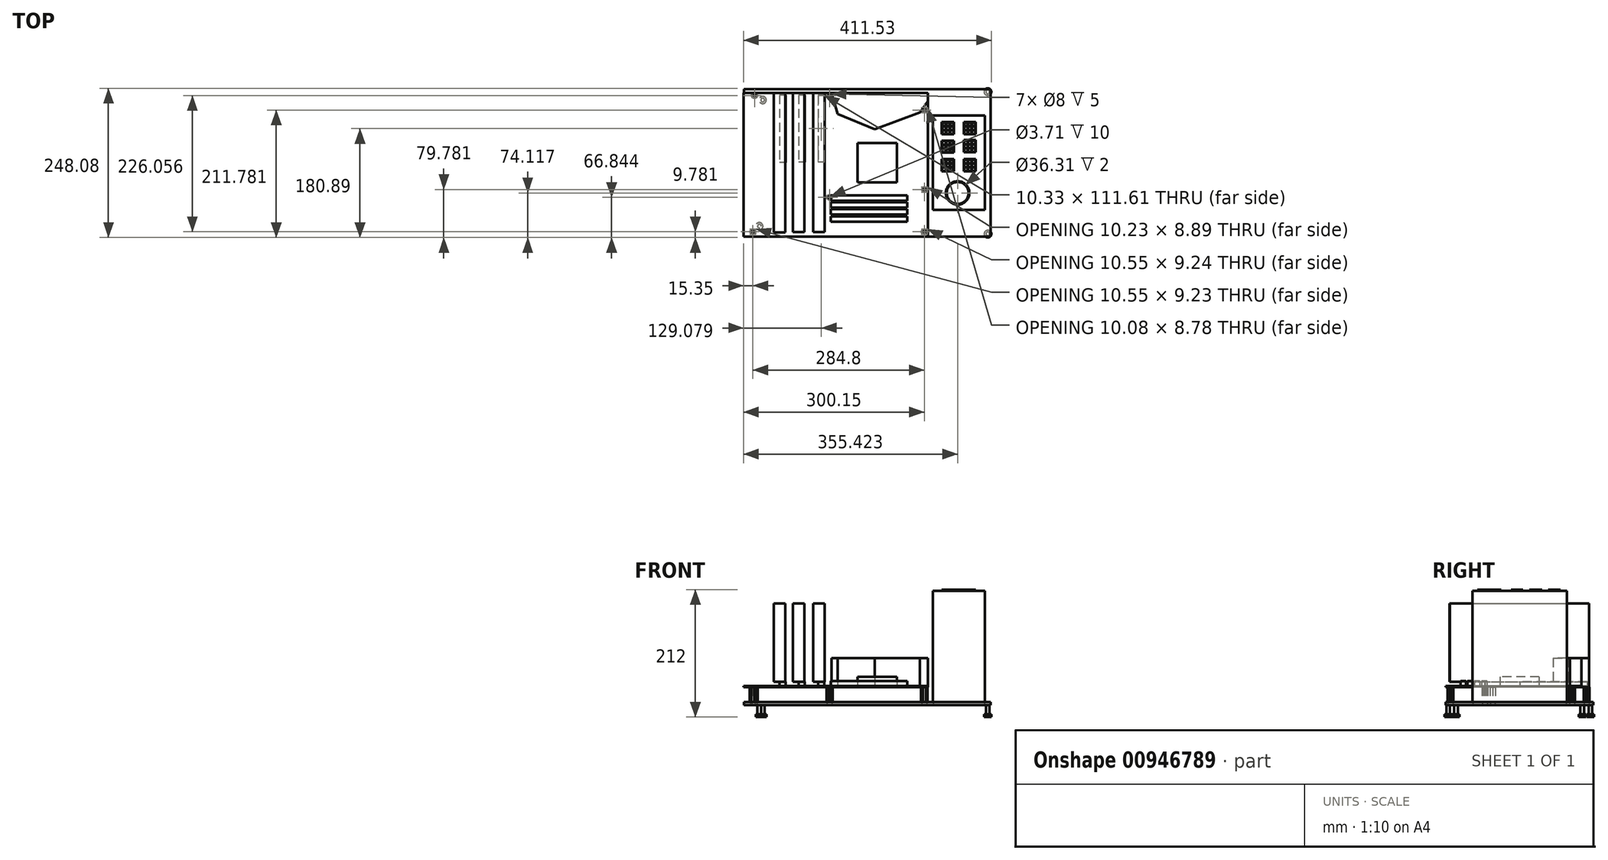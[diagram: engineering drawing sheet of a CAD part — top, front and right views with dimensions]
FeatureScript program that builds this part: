
annotation { "Feature Type Name" : "Feature", "Feature Type Description" : "" }
export const myFeature = defineFeature(function(context is Context, id is Id, definition is map)
    precondition{}
    {
        {
            var Q0;
            Q0=qCreatedBy(makeId("Top.planeOp"),FACE);
            var sketch = newSketch(context, id + "F0", { "sketchPlane" : qUnion([Q0])});
            skLineSegment(sketch, "E0.bottom", {"start": v(-235.28, 113.95) * mm, "end": v(174.52, 113.95) * mm});
            skLineSegment(sketch, "E0.top", {"start": v(-235.28, -131.05) * mm, "end": v(174.52, -131.05) * mm});
            skLineSegment(sketch, "E0.left", {"start": v(-235.28, 113.95) * mm, "end": v(-235.28, -131.05) * mm});
            skLineSegment(sketch, "E0.right", {"start": v(174.52, 113.95) * mm, "end": v(174.52, -131.05) * mm});
            skLineSegment(sketch, "E1", {"start": v(69.52, 113.95) * mm, "end": v(69.52, -131.05) * mm});
            skLineSegment(sketch, "E2.bottom", {"start": v(164.52, 68.95) * mm, "end": v(79.52, 68.95) * mm});
            skLineSegment(sketch, "E2.top", {"start": v(164.52, -86.05) * mm, "end": v(79.52, -86.05) * mm});
            skLineSegment(sketch, "E2.left", {"start": v(164.52, 68.95) * mm, "end": v(164.52, -86.05) * mm});
            skLineSegment(sketch, "E2.right", {"start": v(79.52, 68.95) * mm, "end": v(79.52, -86.05) * mm});
            skCircle(sketch, "E3", {"center": v(-217.38, 103) * mm, "radius": 4 * mm});
            skCircle(sketch, "E4", {"center": v(64.52, 78.95) * mm, "radius": 4 * mm});
            skCircle(sketch, "E5", {"center": v(64.52, -53.05) * mm, "radius": 4 * mm});
            skCircle(sketch, "E6", {"center": v(64.52, -123.05) * mm, "radius": 4 * mm});
            skCircle(sketch, "E7", {"center": v(-92.98, -66.08) * mm, "radius": 4 * mm});
            skCircle(sketch, "E8", {"center": v(-92.98, 103) * mm, "radius": 4 * mm});
            skCircle(sketch, "E9", {"center": v(-220.28, -123.05) * mm, "radius": 4 * mm});
            skCircle(sketch, "E10.cCircle", {"center": v(-92.98, 103) * mm, "radius": 4 * mm, "construction": true});
            skLineSegment(sketch, "E10.0", {"start": v(-88.36, 103.04) * mm, "end": v(-90.64, 99.02) * mm});
            skLineSegment(sketch, "E10.1", {"start": v(-90.64, 99.02) * mm, "end": v(-95.26, 99) * mm});
            skLineSegment(sketch, "E10.2", {"start": v(-95.26, 99) * mm, "end": v(-97.6, 102.98) * mm});
            skLineSegment(sketch, "E10.3", {"start": v(-97.6, 102.98) * mm, "end": v(-95.32, 107) * mm});
            skLineSegment(sketch, "E10.4", {"start": v(-95.32, 107) * mm, "end": v(-90.7, 107.02) * mm});
            skLineSegment(sketch, "E10.5", {"start": v(-90.7, 107.02) * mm, "end": v(-88.36, 103.04) * mm});
            skPoint(sketch, "E10.0.midPoint", {"position": v(-89.5, 101.03) * mm});
            skCircle(sketch, "E11.cCircle", {"center": v(-220.28, -123.05) * mm, "radius": 4 * mm, "construction": true});
            skLineSegment(sketch, "E11.0", {"start": v(-215.66, -123.03) * mm, "end": v(-217.95, -127.04) * mm});
            skLineSegment(sketch, "E11.1", {"start": v(-217.95, -127.04) * mm, "end": v(-222.57, -127.06) * mm});
            skLineSegment(sketch, "E11.2", {"start": v(-222.57, -127.06) * mm, "end": v(-224.9, -123.07) * mm});
            skLineSegment(sketch, "E11.3", {"start": v(-224.9, -123.07) * mm, "end": v(-222.6, -119.06) * mm});
            skLineSegment(sketch, "E11.4", {"start": v(-222.6, -119.06) * mm, "end": v(-217.99, -119.04) * mm});
            skLineSegment(sketch, "E11.5", {"start": v(-217.99, -119.04) * mm, "end": v(-215.66, -123.03) * mm});
            skPoint(sketch, "E11.0.midPoint", {"position": v(-216.8, -125.03) * mm});
            skCircle(sketch, "E12.cCircle", {"center": v(64.52, -123.05) * mm, "radius": 4 * mm, "construction": true});
            skLineSegment(sketch, "E12.0", {"start": v(68.68, -125.06) * mm, "end": v(64.86, -127.66) * mm});
            skLineSegment(sketch, "E12.1", {"start": v(64.86, -127.66) * mm, "end": v(60.7, -125.65) * mm});
            skLineSegment(sketch, "E12.2", {"start": v(60.7, -125.65) * mm, "end": v(60.36, -121.04) * mm});
            skLineSegment(sketch, "E12.3", {"start": v(60.36, -121.04) * mm, "end": v(64.18, -118.44) * mm});
            skLineSegment(sketch, "E12.4", {"start": v(64.18, -118.44) * mm, "end": v(68.34, -120.45) * mm});
            skLineSegment(sketch, "E12.5", {"start": v(68.34, -120.45) * mm, "end": v(68.68, -125.06) * mm});
            skPoint(sketch, "E12.0.midPoint", {"position": v(66.77, -126.36) * mm});
            skCircle(sketch, "E13.cCircle", {"center": v(64.52, -53.05) * mm, "radius": 4 * mm, "construction": true});
            skLineSegment(sketch, "E13.0", {"start": v(66.83, -57.05) * mm, "end": v(62.21, -57.05) * mm});
            skLineSegment(sketch, "E13.1", {"start": v(62.21, -57.05) * mm, "end": v(59.9, -53.05) * mm});
            skLineSegment(sketch, "E13.2", {"start": v(59.9, -53.05) * mm, "end": v(62.21, -49.05) * mm});
            skLineSegment(sketch, "E13.3", {"start": v(62.21, -49.05) * mm, "end": v(66.83, -49.05) * mm});
            skLineSegment(sketch, "E13.4", {"start": v(66.83, -49.05) * mm, "end": v(69.14, -53.05) * mm});
            skLineSegment(sketch, "E13.5", {"start": v(69.14, -53.05) * mm, "end": v(66.83, -57.05) * mm});
            skPoint(sketch, "E13.0.midPoint", {"position": v(64.52, -57.05) * mm});
            skCircle(sketch, "E14.cCircle", {"center": v(64.52, 78.95) * mm, "radius": 4 * mm, "construction": true});
            skLineSegment(sketch, "E14.0", {"start": v(64.04, 74.54) * mm, "end": v(60.77, 76.58) * mm});
            skLineSegment(sketch, "E14.1", {"start": v(60.77, 76.58) * mm, "end": v(60.33, 80.4) * mm});
            skLineSegment(sketch, "E14.2", {"start": v(60.33, 80.4) * mm, "end": v(63.04, 83.14) * mm});
            skLineSegment(sketch, "E14.3", {"start": v(63.04, 83.14) * mm, "end": v(66.87, 82.72) * mm});
            skLineSegment(sketch, "E14.4", {"start": v(66.87, 82.72) * mm, "end": v(68.93, 79.46) * mm});
            skLineSegment(sketch, "E14.5", {"start": v(68.93, 79.46) * mm, "end": v(67.67, 75.82) * mm});
            skLineSegment(sketch, "E14.6", {"start": v(67.67, 75.82) * mm, "end": v(64.04, 74.54) * mm});
            skPoint(sketch, "E14.0.midPoint", {"position": v(62.4, 75.56) * mm});
            skCircle(sketch, "E15.cCircle", {"center": v(-217.38, 103) * mm, "radius": 4 * mm, "construction": true});
            skLineSegment(sketch, "E15.0", {"start": v(-212.76, 102.83) * mm, "end": v(-215.23, 98.92) * mm});
            skLineSegment(sketch, "E15.1", {"start": v(-215.23, 98.92) * mm, "end": v(-219.84, 99.1) * mm});
            skLineSegment(sketch, "E15.2", {"start": v(-219.84, 99.1) * mm, "end": v(-222, 103.19) * mm});
            skLineSegment(sketch, "E15.3", {"start": v(-222, 103.19) * mm, "end": v(-219.53, 107.1) * mm});
            skLineSegment(sketch, "E15.4", {"start": v(-219.53, 107.1) * mm, "end": v(-214.92, 106.91) * mm});
            skLineSegment(sketch, "E15.5", {"start": v(-214.92, 106.91) * mm, "end": v(-212.76, 102.83) * mm});
            skPoint(sketch, "E15.0.midPoint", {"position": v(-214, 100.87) * mm});
            skCircle(sketch, "E16.cCircle", {"center": v(-92.98, -66.08) * mm, "radius": 4 * mm, "construction": true});
            skLineSegment(sketch, "E16.0", {"start": v(-88.36, -66.2) * mm, "end": v(-90.78, -70.14) * mm});
            skLineSegment(sketch, "E16.1", {"start": v(-90.78, -70.14) * mm, "end": v(-95.4, -70.01) * mm});
            skLineSegment(sketch, "E16.2", {"start": v(-95.4, -70.01) * mm, "end": v(-97.6, -65.95) * mm});
            skLineSegment(sketch, "E16.3", {"start": v(-97.6, -65.95) * mm, "end": v(-95.18, -62.02) * mm});
            skLineSegment(sketch, "E16.4", {"start": v(-95.18, -62.02) * mm, "end": v(-90.56, -62.14) * mm});
            skLineSegment(sketch, "E16.5", {"start": v(-90.56, -62.14) * mm, "end": v(-88.36, -66.2) * mm});
            skPoint(sketch, "E16.0.midPoint", {"position": v(-89.57, -68.17) * mm});
            skSolve(sketch);
        }
        {
            var Q0;
            {var subQ0=sQuery(id+"F0.wireOp",EDGE,"E12.4");var subQ1=sQuery(id+"F0.wireOp",EDGE,"E6");var subQ2=makeQuery(id+"F0.imprint","INTERSECT",VERTEX,{"derivedFrom":[subQ1,subQ0]});Q0=makeQuery(id+"F0.imprint","IMPRINT",FACE,{"disambiguationData":[TD([[makeQuery(id+"F0.imprint","IMPRINT",EDGE,{"disambiguationData":[TD([[subQ2,-1.0]])],"derivedFrom":subQ1}),-1.0]])]});}
            var Q1;
            {var subQ0=sQuery(id+"F0.wireOp",EDGE,"E12.3");var subQ1=sQuery(id+"F0.wireOp",EDGE,"E6");var subQ2=makeQuery(id+"F0.imprint","INTERSECT",VERTEX,{"derivedFrom":[subQ1,subQ0]});Q1=makeQuery(id+"F0.imprint","IMPRINT",FACE,{"disambiguationData":[TD([[makeQuery(id+"F0.imprint","IMPRINT",EDGE,{"disambiguationData":[TD([[subQ2,-1.0]])],"derivedFrom":subQ1}),-1.0]])]});}
            var Q2;
            {var subQ0=sQuery(id+"F0.wireOp",EDGE,"E12.1");var subQ1=sQuery(id+"F0.wireOp",EDGE,"E6");var subQ2=makeQuery(id+"F0.imprint","INTERSECT",VERTEX,{"derivedFrom":[subQ1,subQ0]});Q2=makeQuery(id+"F0.imprint","IMPRINT",FACE,{"disambiguationData":[TD([[makeQuery(id+"F0.imprint","IMPRINT",EDGE,{"disambiguationData":[TD([[subQ2,-1.0]])],"derivedFrom":subQ1}),-1.0]])]});}
            var Q3;
            {var subQ0=sQuery(id+"F0.wireOp",EDGE,"E12.5");var subQ1=sQuery(id+"F0.wireOp",EDGE,"E6");var subQ2=makeQuery(id+"F0.imprint","INTERSECT",VERTEX,{"derivedFrom":[subQ1,subQ0]});Q3=makeQuery(id+"F0.imprint","IMPRINT",FACE,{"disambiguationData":[TD([[makeQuery(id+"F0.imprint","IMPRINT",EDGE,{"disambiguationData":[TD([[subQ2,1.0]])],"derivedFrom":subQ1}),-1.0]])]});}
            var Q4;
            {var subQ0=sQuery(id+"F0.wireOp",EDGE,"E12.2");var subQ1=sQuery(id+"F0.wireOp",EDGE,"E6");var subQ2=makeQuery(id+"F0.imprint","INTERSECT",VERTEX,{"derivedFrom":[subQ1,subQ0]});Q4=makeQuery(id+"F0.imprint","IMPRINT",FACE,{"disambiguationData":[TD([[makeQuery(id+"F0.imprint","IMPRINT",EDGE,{"disambiguationData":[TD([[subQ2,-1.0]])],"derivedFrom":subQ1}),-1.0]])]});}
            var Q5;
            {var subQ0=sQuery(id+"F0.wireOp",EDGE,"E12.4");var subQ1=sQuery(id+"F0.wireOp",EDGE,"E6");var subQ2=makeQuery(id+"F0.imprint","INTERSECT",VERTEX,{"derivedFrom":[subQ1,subQ0]});Q5=makeQuery(id+"F0.imprint","IMPRINT",FACE,{"disambiguationData":[TD([[makeQuery(id+"F0.imprint","IMPRINT",EDGE,{"disambiguationData":[TD([[subQ2,1.0]])],"derivedFrom":subQ1}),-1.0]])]});}
            var Q6;
            {var subQ0=sQuery(id+"F0.wireOp",EDGE,"E16.4");var subQ1=sQuery(id+"F0.wireOp",EDGE,"E7");var subQ2=makeQuery(id+"F0.imprint","INTERSECT",VERTEX,{"derivedFrom":[subQ1,subQ0]});Q6=makeQuery(id+"F0.imprint","IMPRINT",FACE,{"disambiguationData":[TD([[makeQuery(id+"F0.imprint","IMPRINT",EDGE,{"disambiguationData":[TD([[subQ2,1.0]])],"derivedFrom":subQ1}),-1.0]])]});}
            var Q7;
            {var subQ0=sQuery(id+"F0.wireOp",EDGE,"E16.4");var subQ1=sQuery(id+"F0.wireOp",EDGE,"E7");var subQ2=makeQuery(id+"F0.imprint","INTERSECT",VERTEX,{"derivedFrom":[subQ1,subQ0]});Q7=makeQuery(id+"F0.imprint","IMPRINT",FACE,{"disambiguationData":[TD([[makeQuery(id+"F0.imprint","IMPRINT",EDGE,{"disambiguationData":[TD([[subQ2,-1.0]])],"derivedFrom":subQ1}),-1.0]])]});}
            var Q8;
            {var subQ0=sQuery(id+"F0.wireOp",EDGE,"E16.3");var subQ1=sQuery(id+"F0.wireOp",EDGE,"E7");var subQ2=makeQuery(id+"F0.imprint","INTERSECT",VERTEX,{"derivedFrom":[subQ1,subQ0]});Q8=makeQuery(id+"F0.imprint","IMPRINT",FACE,{"disambiguationData":[TD([[makeQuery(id+"F0.imprint","IMPRINT",EDGE,{"disambiguationData":[TD([[subQ2,-1.0]])],"derivedFrom":subQ1}),-1.0]])]});}
            var Q9;
            {var subQ0=sQuery(id+"F0.wireOp",EDGE,"E16.2");var subQ1=sQuery(id+"F0.wireOp",EDGE,"E7");var subQ2=makeQuery(id+"F0.imprint","INTERSECT",VERTEX,{"derivedFrom":[subQ1,subQ0]});Q9=makeQuery(id+"F0.imprint","IMPRINT",FACE,{"disambiguationData":[TD([[makeQuery(id+"F0.imprint","IMPRINT",EDGE,{"disambiguationData":[TD([[subQ2,-1.0]])],"derivedFrom":subQ1}),-1.0]])]});}
            var Q10;
            {var subQ0=sQuery(id+"F0.wireOp",EDGE,"E16.1");var subQ1=sQuery(id+"F0.wireOp",EDGE,"E7");var subQ2=makeQuery(id+"F0.imprint","INTERSECT",VERTEX,{"derivedFrom":[subQ1,subQ0]});Q10=makeQuery(id+"F0.imprint","IMPRINT",FACE,{"disambiguationData":[TD([[makeQuery(id+"F0.imprint","IMPRINT",EDGE,{"disambiguationData":[TD([[subQ2,-1.0]])],"derivedFrom":subQ1}),-1.0]])]});}
            var Q11;
            {var subQ0=sQuery(id+"F0.wireOp",EDGE,"E16.5");var subQ1=sQuery(id+"F0.wireOp",EDGE,"E7");var subQ2=makeQuery(id+"F0.imprint","INTERSECT",VERTEX,{"derivedFrom":[subQ1,subQ0]});Q11=makeQuery(id+"F0.imprint","IMPRINT",FACE,{"disambiguationData":[TD([[makeQuery(id+"F0.imprint","IMPRINT",EDGE,{"disambiguationData":[TD([[subQ2,1.0]])],"derivedFrom":subQ1}),-1.0]])]});}
            var Q12;
            {var subQ0=sQuery(id+"F0.wireOp",EDGE,"E11.1");var subQ1=sQuery(id+"F0.wireOp",EDGE,"E9");var subQ2=makeQuery(id+"F0.imprint","INTERSECT",VERTEX,{"derivedFrom":[subQ1,subQ0]});Q12=makeQuery(id+"F0.imprint","IMPRINT",FACE,{"disambiguationData":[TD([[makeQuery(id+"F0.imprint","IMPRINT",EDGE,{"disambiguationData":[TD([[subQ2,-1.0]])],"derivedFrom":subQ1}),-1.0]])]});}
            var Q13;
            {var subQ0=sQuery(id+"F0.wireOp",EDGE,"E11.5");var subQ1=sQuery(id+"F0.wireOp",EDGE,"E9");var subQ2=makeQuery(id+"F0.imprint","INTERSECT",VERTEX,{"derivedFrom":[subQ1,subQ0]});Q13=makeQuery(id+"F0.imprint","IMPRINT",FACE,{"disambiguationData":[TD([[makeQuery(id+"F0.imprint","IMPRINT",EDGE,{"disambiguationData":[TD([[subQ2,1.0]])],"derivedFrom":subQ1}),-1.0]])]});}
            var Q14;
            {var subQ0=sQuery(id+"F0.wireOp",EDGE,"E11.4");var subQ1=sQuery(id+"F0.wireOp",EDGE,"E9");var subQ2=makeQuery(id+"F0.imprint","INTERSECT",VERTEX,{"derivedFrom":[subQ1,subQ0]});Q14=makeQuery(id+"F0.imprint","IMPRINT",FACE,{"disambiguationData":[TD([[makeQuery(id+"F0.imprint","IMPRINT",EDGE,{"disambiguationData":[TD([[subQ2,1.0]])],"derivedFrom":subQ1}),-1.0]])]});}
            var Q15;
            {var subQ0=sQuery(id+"F0.wireOp",EDGE,"E11.4");var subQ1=sQuery(id+"F0.wireOp",EDGE,"E9");var subQ2=makeQuery(id+"F0.imprint","INTERSECT",VERTEX,{"derivedFrom":[subQ1,subQ0]});Q15=makeQuery(id+"F0.imprint","IMPRINT",FACE,{"disambiguationData":[TD([[makeQuery(id+"F0.imprint","IMPRINT",EDGE,{"disambiguationData":[TD([[subQ2,-1.0]])],"derivedFrom":subQ1}),-1.0]])]});}
            var Q16;
            {var subQ0=sQuery(id+"F0.wireOp",EDGE,"E11.3");var subQ1=sQuery(id+"F0.wireOp",EDGE,"E9");var subQ2=makeQuery(id+"F0.imprint","INTERSECT",VERTEX,{"derivedFrom":[subQ1,subQ0]});Q16=makeQuery(id+"F0.imprint","IMPRINT",FACE,{"disambiguationData":[TD([[makeQuery(id+"F0.imprint","IMPRINT",EDGE,{"disambiguationData":[TD([[subQ2,-1.0]])],"derivedFrom":subQ1}),-1.0]])]});}
            var Q17;
            {var subQ0=sQuery(id+"F0.wireOp",EDGE,"E11.2");var subQ1=sQuery(id+"F0.wireOp",EDGE,"E9");var subQ2=makeQuery(id+"F0.imprint","INTERSECT",VERTEX,{"derivedFrom":[subQ1,subQ0]});Q17=makeQuery(id+"F0.imprint","IMPRINT",FACE,{"disambiguationData":[TD([[makeQuery(id+"F0.imprint","IMPRINT",EDGE,{"disambiguationData":[TD([[subQ2,-1.0]])],"derivedFrom":subQ1}),-1.0]])]});}
            var Q18;
            {var subQ0=sQuery(id+"F0.wireOp",EDGE,"E15.4");var subQ1=sQuery(id+"F0.wireOp",EDGE,"E3");var subQ2=makeQuery(id+"F0.imprint","INTERSECT",VERTEX,{"derivedFrom":[subQ1,subQ0]});Q18=makeQuery(id+"F0.imprint","IMPRINT",FACE,{"disambiguationData":[TD([[makeQuery(id+"F0.imprint","IMPRINT",EDGE,{"disambiguationData":[TD([[subQ2,-1.0]])],"derivedFrom":subQ1}),-1.0]])]});}
            var Q19;
            {var subQ0=sQuery(id+"F0.wireOp",EDGE,"E15.1");var subQ1=sQuery(id+"F0.wireOp",EDGE,"E3");var subQ2=makeQuery(id+"F0.imprint","INTERSECT",VERTEX,{"derivedFrom":[subQ1,subQ0]});Q19=makeQuery(id+"F0.imprint","IMPRINT",FACE,{"disambiguationData":[TD([[makeQuery(id+"F0.imprint","IMPRINT",EDGE,{"disambiguationData":[TD([[subQ2,-1.0]])],"derivedFrom":subQ1}),-1.0]])]});}
            var Q20;
            {var subQ0=sQuery(id+"F0.wireOp",EDGE,"E15.5");var subQ1=sQuery(id+"F0.wireOp",EDGE,"E3");var subQ2=makeQuery(id+"F0.imprint","INTERSECT",VERTEX,{"derivedFrom":[subQ1,subQ0]});Q20=makeQuery(id+"F0.imprint","IMPRINT",FACE,{"disambiguationData":[TD([[makeQuery(id+"F0.imprint","IMPRINT",EDGE,{"disambiguationData":[TD([[subQ2,1.0]])],"derivedFrom":subQ1}),-1.0]])]});}
            var Q21;
            {var subQ0=sQuery(id+"F0.wireOp",EDGE,"E15.4");var subQ1=sQuery(id+"F0.wireOp",EDGE,"E3");var subQ2=makeQuery(id+"F0.imprint","INTERSECT",VERTEX,{"derivedFrom":[subQ1,subQ0]});Q21=makeQuery(id+"F0.imprint","IMPRINT",FACE,{"disambiguationData":[TD([[makeQuery(id+"F0.imprint","IMPRINT",EDGE,{"disambiguationData":[TD([[subQ2,1.0]])],"derivedFrom":subQ1}),-1.0]])]});}
            var Q22;
            {var subQ0=sQuery(id+"F0.wireOp",EDGE,"E14.3");var subQ1=sQuery(id+"F0.wireOp",EDGE,"E4");var subQ2=makeQuery(id+"F0.imprint","INTERSECT",VERTEX,{"derivedFrom":[subQ1,subQ0]});Q22=makeQuery(id+"F0.imprint","IMPRINT",FACE,{"disambiguationData":[TD([[makeQuery(id+"F0.imprint","IMPRINT",EDGE,{"disambiguationData":[TD([[subQ2,-1.0]])],"derivedFrom":subQ1}),-1.0]])]});}
            var Q23;
            {var subQ0=sQuery(id+"F0.wireOp",EDGE,"E14.2");var subQ1=sQuery(id+"F0.wireOp",EDGE,"E4");var subQ2=makeQuery(id+"F0.imprint","INTERSECT",VERTEX,{"derivedFrom":[subQ1,subQ0]});Q23=makeQuery(id+"F0.imprint","IMPRINT",FACE,{"disambiguationData":[TD([[makeQuery(id+"F0.imprint","IMPRINT",EDGE,{"disambiguationData":[TD([[subQ2,-1.0]])],"derivedFrom":subQ1}),-1.0]])]});}
            var Q24;
            {var subQ0=sQuery(id+"F0.wireOp",EDGE,"E14.1");var subQ1=sQuery(id+"F0.wireOp",EDGE,"E4");var subQ2=makeQuery(id+"F0.imprint","INTERSECT",VERTEX,{"derivedFrom":[subQ1,subQ0]});Q24=makeQuery(id+"F0.imprint","IMPRINT",FACE,{"disambiguationData":[TD([[makeQuery(id+"F0.imprint","IMPRINT",EDGE,{"disambiguationData":[TD([[subQ2,-1.0]])],"derivedFrom":subQ1}),-1.0]])]});}
            var Q25;
            {var subQ10=sQuery(id+"F0.wireOp",EDGE,"E0.right");Q25=makeQuery(id+"F0.imprint","IMPRINT",FACE,{"disambiguationData":[TD([[makeQuery(id+"F0.imprint","IMPRINT",EDGE,{"derivedFrom":subQ10}),-1.0]])]});}
            var Q26;
            {var subQ0=sQuery(id+"F0.wireOp",EDGE,"E14.6");var subQ1=sQuery(id+"F0.wireOp",EDGE,"E4");var subQ2=makeQuery(id+"F0.imprint","INTERSECT",VERTEX,{"derivedFrom":[subQ1,subQ0]});Q26=makeQuery(id+"F0.imprint","IMPRINT",FACE,{"disambiguationData":[TD([[makeQuery(id+"F0.imprint","IMPRINT",EDGE,{"disambiguationData":[TD([[subQ2,-1.0]])],"derivedFrom":subQ1}),-1.0]])]});}
            var Q27;
            {var subQ0=sQuery(id+"F0.wireOp",EDGE,"E14.4");var subQ1=sQuery(id+"F0.wireOp",EDGE,"E4");var subQ2=makeQuery(id+"F0.imprint","INTERSECT",VERTEX,{"derivedFrom":[subQ1,subQ0]});Q27=makeQuery(id+"F0.imprint","IMPRINT",FACE,{"disambiguationData":[TD([[makeQuery(id+"F0.imprint","IMPRINT",EDGE,{"disambiguationData":[TD([[subQ2,1.0]])],"derivedFrom":subQ1}),-1.0]])]});}
            var Q28;
            {var subQ0=sQuery(id+"F0.wireOp",EDGE,"E14.3");var subQ1=sQuery(id+"F0.wireOp",EDGE,"E4");var subQ2=makeQuery(id+"F0.imprint","INTERSECT",VERTEX,{"derivedFrom":[subQ1,subQ0]});Q28=makeQuery(id+"F0.imprint","IMPRINT",FACE,{"disambiguationData":[TD([[makeQuery(id+"F0.imprint","IMPRINT",EDGE,{"disambiguationData":[TD([[subQ2,1.0]])],"derivedFrom":subQ1}),-1.0]])]});}
            var Q29;
            {var subQ7=sQuery(id+"F0.wireOp",EDGE,"E0.left");Q29=makeQuery(id+"F0.imprint","IMPRINT",FACE,{"disambiguationData":[TD([[makeQuery(id+"F0.imprint","IMPRINT",EDGE,{"derivedFrom":subQ7}),1.0]])]});}
            var Q30;
            {var subQ0=sQuery(id+"F0.wireOp",EDGE,"E14.0");var subQ1=sQuery(id+"F0.wireOp",EDGE,"E4");var subQ2=makeQuery(id+"F0.imprint","INTERSECT",VERTEX,{"derivedFrom":[subQ1,subQ0]});Q30=makeQuery(id+"F0.imprint","IMPRINT",FACE,{"disambiguationData":[TD([[makeQuery(id+"F0.imprint","IMPRINT",EDGE,{"disambiguationData":[TD([[subQ2,-1.0]])],"derivedFrom":subQ1}),-1.0]])]});}
            var Q31;
            {var subQ0=sQuery(id+"F0.wireOp",EDGE,"E13.3");var subQ1=sQuery(id+"F0.wireOp",EDGE,"E5");var subQ2=makeQuery(id+"F0.imprint","INTERSECT",VERTEX,{"derivedFrom":[subQ1,subQ0]});Q31=makeQuery(id+"F0.imprint","IMPRINT",FACE,{"disambiguationData":[TD([[makeQuery(id+"F0.imprint","IMPRINT",EDGE,{"disambiguationData":[TD([[subQ2,1.0]])],"derivedFrom":subQ1}),-1.0]])]});}
            var Q32;
            {var subQ0=sQuery(id+"F0.wireOp",EDGE,"E13.4");var subQ1=sQuery(id+"F0.wireOp",EDGE,"E5");var subQ2=makeQuery(id+"F0.imprint","INTERSECT",VERTEX,{"derivedFrom":[subQ1,subQ0]});Q32=makeQuery(id+"F0.imprint","IMPRINT",FACE,{"disambiguationData":[TD([[makeQuery(id+"F0.imprint","IMPRINT",EDGE,{"disambiguationData":[TD([[subQ2,1.0]])],"derivedFrom":subQ1}),-1.0]])]});}
            var Q33;
            {var subQ0=sQuery(id+"F0.wireOp",EDGE,"E13.0");var subQ1=sQuery(id+"F0.wireOp",EDGE,"E5");var subQ2=makeQuery(id+"F0.imprint","INTERSECT",VERTEX,{"derivedFrom":[subQ1,subQ0]});Q33=makeQuery(id+"F0.imprint","IMPRINT",FACE,{"disambiguationData":[TD([[makeQuery(id+"F0.imprint","IMPRINT",EDGE,{"disambiguationData":[TD([[subQ2,-1.0]])],"derivedFrom":subQ1}),-1.0]])]});}
            var Q34;
            {var subQ0=sQuery(id+"F0.wireOp",EDGE,"E13.1");var subQ1=sQuery(id+"F0.wireOp",EDGE,"E5");var subQ2=makeQuery(id+"F0.imprint","INTERSECT",VERTEX,{"derivedFrom":[subQ1,subQ0]});Q34=makeQuery(id+"F0.imprint","IMPRINT",FACE,{"disambiguationData":[TD([[makeQuery(id+"F0.imprint","IMPRINT",EDGE,{"disambiguationData":[TD([[subQ2,-1.0]])],"derivedFrom":subQ1}),-1.0]])]});}
            var Q35;
            {var subQ0=sQuery(id+"F0.wireOp",EDGE,"E13.2");var subQ1=sQuery(id+"F0.wireOp",EDGE,"E5");var subQ2=makeQuery(id+"F0.imprint","INTERSECT",VERTEX,{"derivedFrom":[subQ1,subQ0]});Q35=makeQuery(id+"F0.imprint","IMPRINT",FACE,{"disambiguationData":[TD([[makeQuery(id+"F0.imprint","IMPRINT",EDGE,{"disambiguationData":[TD([[subQ2,-1.0]])],"derivedFrom":subQ1}),-1.0]])]});}
            var Q36;
            {var subQ0=sQuery(id+"F0.wireOp",EDGE,"E13.3");var subQ1=sQuery(id+"F0.wireOp",EDGE,"E5");var subQ2=makeQuery(id+"F0.imprint","INTERSECT",VERTEX,{"derivedFrom":[subQ1,subQ0]});Q36=makeQuery(id+"F0.imprint","IMPRINT",FACE,{"disambiguationData":[TD([[makeQuery(id+"F0.imprint","IMPRINT",EDGE,{"disambiguationData":[TD([[subQ2,-1.0]])],"derivedFrom":subQ1}),-1.0]])]});}
            var Q37;
            {var subQ0=sQuery(id+"F0.wireOp",EDGE,"fnGGJgAr-T0BG-MF3t-gyGZ-hbNT0MP3fvNB");Q37=makeQuery(id+"F0.imprint","IMPRINT",FACE,{"disambiguationData":[TD([[makeQuery(id+"F0.imprint","IMPRINT",EDGE,{"derivedFrom":subQ0}),1.0]])]});}
            var Q38;
            {var subQ4=sQuery(id+"F0.wireOp",EDGE,"iKlQyD2N-WRxG-utMa-lJ8L-cIOPaJfjkMKQ");Q38=makeQuery(id+"F0.imprint","IMPRINT",FACE,{"disambiguationData":[TD([[makeQuery(id+"F0.imprint","IMPRINT",EDGE,{"derivedFrom":subQ4}),-1.0]])]});}
            var Q39;
            {var subQ0=sQuery(id+"F0.wireOp",EDGE,"E10.2");var subQ1=sQuery(id+"F0.wireOp",EDGE,"E8");var subQ2=makeQuery(id+"F0.imprint","INTERSECT",VERTEX,{"derivedFrom":[subQ1,subQ0]});Q39=makeQuery(id+"F0.imprint","IMPRINT",FACE,{"disambiguationData":[TD([[makeQuery(id+"F0.imprint","IMPRINT",EDGE,{"disambiguationData":[TD([[subQ2,-1.0]])],"derivedFrom":subQ1}),-1.0]])]});}
            var Q40;
            {var subQ0=sQuery(id+"F0.wireOp",EDGE,"E10.1");var subQ1=sQuery(id+"F0.wireOp",EDGE,"E8");var subQ2=makeQuery(id+"F0.imprint","INTERSECT",VERTEX,{"derivedFrom":[subQ1,subQ0]});Q40=makeQuery(id+"F0.imprint","IMPRINT",FACE,{"disambiguationData":[TD([[makeQuery(id+"F0.imprint","IMPRINT",EDGE,{"disambiguationData":[TD([[subQ2,-1.0]])],"derivedFrom":subQ1}),-1.0]])]});}
            var Q41;
            {var subQ0=sQuery(id+"F0.wireOp",EDGE,"E10.5");var subQ1=sQuery(id+"F0.wireOp",EDGE,"E8");var subQ2=makeQuery(id+"F0.imprint","INTERSECT",VERTEX,{"derivedFrom":[subQ1,subQ0]});Q41=makeQuery(id+"F0.imprint","IMPRINT",FACE,{"disambiguationData":[TD([[makeQuery(id+"F0.imprint","IMPRINT",EDGE,{"disambiguationData":[TD([[subQ2,1.0]])],"derivedFrom":subQ1}),-1.0]])]});}
            var Q42;
            {var subQ0=sQuery(id+"F0.wireOp",EDGE,"E10.4");var subQ1=sQuery(id+"F0.wireOp",EDGE,"E8");var subQ2=makeQuery(id+"F0.imprint","INTERSECT",VERTEX,{"derivedFrom":[subQ1,subQ0]});Q42=makeQuery(id+"F0.imprint","IMPRINT",FACE,{"disambiguationData":[TD([[makeQuery(id+"F0.imprint","IMPRINT",EDGE,{"disambiguationData":[TD([[subQ2,1.0]])],"derivedFrom":subQ1}),-1.0]])]});}
            var Q43;
            {var subQ0=sQuery(id+"F0.wireOp",EDGE,"E10.4");var subQ1=sQuery(id+"F0.wireOp",EDGE,"E8");var subQ2=makeQuery(id+"F0.imprint","INTERSECT",VERTEX,{"derivedFrom":[subQ1,subQ0]});Q43=makeQuery(id+"F0.imprint","IMPRINT",FACE,{"disambiguationData":[TD([[makeQuery(id+"F0.imprint","IMPRINT",EDGE,{"disambiguationData":[TD([[subQ2,-1.0]])],"derivedFrom":subQ1}),-1.0]])]});}
            var Q44;
            {var subQ0=sQuery(id+"F0.wireOp",EDGE,"E10.3");var subQ1=sQuery(id+"F0.wireOp",EDGE,"E8");var subQ2=makeQuery(id+"F0.imprint","INTERSECT",VERTEX,{"derivedFrom":[subQ1,subQ0]});Q44=makeQuery(id+"F0.imprint","IMPRINT",FACE,{"disambiguationData":[TD([[makeQuery(id+"F0.imprint","IMPRINT",EDGE,{"disambiguationData":[TD([[subQ2,-1.0]])],"derivedFrom":subQ1}),-1.0]])]});}
            var Q45;
            {var subQ0=sQuery(id+"F0.wireOp",EDGE,"E15.2");var subQ1=sQuery(id+"F0.wireOp",EDGE,"E3");var subQ2=makeQuery(id+"F0.imprint","INTERSECT",VERTEX,{"derivedFrom":[subQ1,subQ0]});Q45=makeQuery(id+"F0.imprint","IMPRINT",FACE,{"disambiguationData":[TD([[makeQuery(id+"F0.imprint","IMPRINT",EDGE,{"disambiguationData":[TD([[subQ2,-1.0]])],"derivedFrom":subQ1}),-1.0]])]});}
            var Q46;
            {var subQ0=sQuery(id+"F0.wireOp",EDGE,"E15.3");var subQ1=sQuery(id+"F0.wireOp",EDGE,"E3");var subQ2=makeQuery(id+"F0.imprint","INTERSECT",VERTEX,{"derivedFrom":[subQ1,subQ0]});Q46=makeQuery(id+"F0.imprint","IMPRINT",FACE,{"disambiguationData":[TD([[makeQuery(id+"F0.imprint","IMPRINT",EDGE,{"disambiguationData":[TD([[subQ2,-1.0]])],"derivedFrom":subQ1}),-1.0]])]});}
            extrude(context, id + "F1", {"entities" : qUnion([Q0, Q1, Q2, Q3, Q4, Q5, Q6, Q7, Q8, Q9, Q10, Q11, Q12, Q13, Q14, Q15, Q16, Q17, Q18, Q19, Q20, Q21, Q22, Q23, Q24, Q25, Q26, Q27, Q28, Q29, Q30, Q31, Q32, Q33, Q34, Q35, Q36, Q37, Q38, Q39, Q40, Q41, Q42, Q43, Q44, Q45, Q46]), "depth" : 5 * mm, "offsetDistance" : 25 * mm});
        }
        {
            var Q0;
            Q0=makeQuery(id+"F1.opExtrude","SWEPT_EDGE",EDGE,{"disambiguationData":[OSD([sQuery(id+"F0.wireOp",EDGE,"iKlQyD2N-WRxG-utMa-lJ8L-cIOPaJfjkMKQ"),sQuery(id+"F0.wireOp",EDGE,"8L1Znl8v-4MLT-wmsx-H5cy-UTvKXKrOukI6")])]});
            var Q1;
            Q1=makeQuery(id+"F1.opExtrude","SWEPT_EDGE",EDGE,{"disambiguationData":[OSD([sQuery(id+"F0.wireOp",EDGE,"E2.bottom"),sQuery(id+"F0.wireOp",EDGE,"8L1Znl8v-4MLT-wmsx-H5cy-UTvKXKrOukI6")])]});
            var Q2;
            Q2=makeQuery(id+"F1.opExtrude","SWEPT_EDGE",EDGE,{"disambiguationData":[OSD([sQuery(id+"F0.wireOp",EDGE,"E2.left"),sQuery(id+"F0.wireOp",EDGE,"iKlQyD2N-WRxG-utMa-lJ8L-cIOPaJfjkMKQ")])]});
            fillet(context, id + "F2", {"entities" : qUnion([Q0, Q1, Q2]), "radius" : 2 * mm, "tangentPropagation" : true, "allowEdgeOverflow" : false});
        }
        {
            var Q0;
            Q0=makeQuery(id+"F1.opExtrude","CAP_FACE",FACE,{"disambiguationData":[OSD([sQuery(id+"F0.wireOp",EDGE,"E0.bottom"),sQuery(id+"F0.wireOp",EDGE,"E0.top"),sQuery(id+"F0.wireOp",EDGE,"E0.left"),sQuery(id+"F0.wireOp",EDGE,"E0.right"),sQuery(id+"F0.wireOp",EDGE,"E2.bottom"),sQuery(id+"F0.wireOp",EDGE,"E2.top"),sQuery(id+"F0.wireOp",EDGE,"E2.left"),sQuery(id+"F0.wireOp",EDGE,"E2.right"),sQuery(id+"F0.wireOp",EDGE,"iKlQyD2N-WRxG-utMa-lJ8L-cIOPaJfjkMKQ"),sQuery(id+"F0.wireOp",EDGE,"8L1Znl8v-4MLT-wmsx-H5cy-UTvKXKrOukI6"),sQuery(id+"F0.wireOp",EDGE,"fnGGJgAr-T0BG-MF3t-gyGZ-hbNT0MP3fvNB"),sQuery(id+"F0.wireOp",EDGE,"E3"),sQuery(id+"F0.wireOp",EDGE,"E4"),sQuery(id+"F0.wireOp",EDGE,"E5"),sQuery(id+"F0.wireOp",EDGE,"E6"),sQuery(id+"F0.wireOp",EDGE,"E7"),sQuery(id+"F0.wireOp",EDGE,"E8"),sQuery(id+"F0.wireOp",EDGE,"E9")])],"isStart":false});
            var sketch = newSketch(context, id + "F3", { "sketchPlane" : qUnion([Q0])});
            skCircle(sketch, "E17.cCircle", {"center": v(-92.98, -66.08) * mm, "radius": 4.44 * mm, "construction": true});
            skLineSegment(sketch, "E17.0", {"start": v(-88.26, -67) * mm, "end": v(-90.3, -70.07) * mm});
            skLineSegment(sketch, "E17.1", {"start": v(-90.3, -70.07) * mm, "end": v(-93.9, -70.8) * mm});
            skLineSegment(sketch, "E17.2", {"start": v(-93.9, -70.8) * mm, "end": v(-96.97, -68.76) * mm});
            skLineSegment(sketch, "E17.3", {"start": v(-96.97, -68.76) * mm, "end": v(-97.7, -65.15) * mm});
            skLineSegment(sketch, "E17.4", {"start": v(-97.7, -65.15) * mm, "end": v(-95.66, -62.09) * mm});
            skLineSegment(sketch, "E17.5", {"start": v(-95.66, -62.09) * mm, "end": v(-92.05, -61.36) * mm});
            skLineSegment(sketch, "E17.6", {"start": v(-92.05, -61.36) * mm, "end": v(-88.99, -63.4) * mm});
            skLineSegment(sketch, "E17.7", {"start": v(-88.99, -63.4) * mm, "end": v(-88.26, -67) * mm});
            skPoint(sketch, "E17.0.midPoint", {"position": v(-89.28, -68.54) * mm});
            skCircle(sketch, "E18.cCircle", {"center": v(64.52, 78.95) * mm, "radius": 4.36 * mm, "construction": true});
            skLineSegment(sketch, "E18.0", {"start": v(69.56, 79) * mm, "end": v(67.08, 74.6) * mm});
            skLineSegment(sketch, "E18.1", {"start": v(67.08, 74.6) * mm, "end": v(62.04, 74.56) * mm});
            skLineSegment(sketch, "E18.2", {"start": v(62.04, 74.56) * mm, "end": v(59.48, 78.9) * mm});
            skLineSegment(sketch, "E18.3", {"start": v(59.48, 78.9) * mm, "end": v(61.96, 83.3) * mm});
            skLineSegment(sketch, "E18.4", {"start": v(61.96, 83.3) * mm, "end": v(67, 83.34) * mm});
            skLineSegment(sketch, "E18.5", {"start": v(67, 83.34) * mm, "end": v(69.56, 79) * mm});
            skPoint(sketch, "E18.0.midPoint", {"position": v(68.32, 76.8) * mm});
            skCircle(sketch, "E19.cCircle", {"center": v(-92.98, 103) * mm, "radius": 4.4 * mm, "construction": true});
            skLineSegment(sketch, "E19.0", {"start": v(-87.9, 103.05) * mm, "end": v(-90.4, 98.63) * mm});
            skLineSegment(sketch, "E19.1", {"start": v(-90.4, 98.63) * mm, "end": v(-95.48, 98.59) * mm});
            skLineSegment(sketch, "E19.2", {"start": v(-95.48, 98.59) * mm, "end": v(-98.06, 102.96) * mm});
            skLineSegment(sketch, "E19.3", {"start": v(-98.06, 102.96) * mm, "end": v(-95.56, 107.38) * mm});
            skLineSegment(sketch, "E19.4", {"start": v(-95.56, 107.38) * mm, "end": v(-90.48, 107.43) * mm});
            skLineSegment(sketch, "E19.5", {"start": v(-90.48, 107.43) * mm, "end": v(-87.9, 103.05) * mm});
            skPoint(sketch, "E19.0.midPoint", {"position": v(-89.15, 100.84) * mm});
            skCircle(sketch, "E20.cCircle", {"center": v(-217.38, 103) * mm, "radius": 4.62 * mm, "construction": true});
            skLineSegment(sketch, "E20.0", {"start": v(-212.04, 102.95) * mm, "end": v(-214.76, 98.36) * mm});
            skLineSegment(sketch, "E20.1", {"start": v(-214.76, 98.36) * mm, "end": v(-220.1, 98.41) * mm});
            skLineSegment(sketch, "E20.2", {"start": v(-220.1, 98.41) * mm, "end": v(-222.72, 103.06) * mm});
            skLineSegment(sketch, "E20.3", {"start": v(-222.72, 103.06) * mm, "end": v(-220, 107.65) * mm});
            skLineSegment(sketch, "E20.4", {"start": v(-220, 107.65) * mm, "end": v(-214.67, 107.6) * mm});
            skLineSegment(sketch, "E20.5", {"start": v(-214.67, 107.6) * mm, "end": v(-212.04, 102.95) * mm});
            skPoint(sketch, "E20.0.midPoint", {"position": v(-213.4, 100.66) * mm});
            skCircle(sketch, "E21.cCircle", {"center": v(-220.28, -123.05) * mm, "radius": 4.57 * mm, "construction": true});
            skLineSegment(sketch, "E21.0", {"start": v(-215, -122.95) * mm, "end": v(-217.55, -127.56) * mm});
            skLineSegment(sketch, "E21.1", {"start": v(-217.55, -127.56) * mm, "end": v(-222.83, -127.67) * mm});
            skLineSegment(sketch, "E21.2", {"start": v(-222.83, -127.67) * mm, "end": v(-225.55, -123.15) * mm});
            skLineSegment(sketch, "E21.3", {"start": v(-225.55, -123.15) * mm, "end": v(-223, -118.53) * mm});
            skLineSegment(sketch, "E21.4", {"start": v(-223, -118.53) * mm, "end": v(-217.73, -118.43) * mm});
            skLineSegment(sketch, "E21.5", {"start": v(-217.73, -118.43) * mm, "end": v(-215, -122.95) * mm});
            skPoint(sketch, "E21.0.midPoint", {"position": v(-216.28, -125.26) * mm});
            skCircle(sketch, "E22.cCircle", {"center": v(64.52, -123.05) * mm, "radius": 4.57 * mm, "construction": true});
            skLineSegment(sketch, "E22.0", {"start": v(69.8, -122.95) * mm, "end": v(67.25, -127.57) * mm});
            skLineSegment(sketch, "E22.1", {"start": v(67.25, -127.57) * mm, "end": v(61.97, -127.67) * mm});
            skLineSegment(sketch, "E22.2", {"start": v(61.97, -127.67) * mm, "end": v(59.24, -123.15) * mm});
            skLineSegment(sketch, "E22.3", {"start": v(59.24, -123.15) * mm, "end": v(61.8, -118.53) * mm});
            skLineSegment(sketch, "E22.4", {"start": v(61.8, -118.53) * mm, "end": v(67.07, -118.43) * mm});
            skLineSegment(sketch, "E22.5", {"start": v(67.07, -118.43) * mm, "end": v(69.8, -122.95) * mm});
            skPoint(sketch, "E22.0.midPoint", {"position": v(68.52, -125.26) * mm});
            skCircle(sketch, "E23.cCircle", {"center": v(64.52, -53.05) * mm, "radius": 4.43 * mm, "construction": true});
            skLineSegment(sketch, "E23.0", {"start": v(69.63, -53.01) * mm, "end": v(67.11, -57.46) * mm});
            skLineSegment(sketch, "E23.1", {"start": v(67.11, -57.46) * mm, "end": v(62, -57.5) * mm});
            skLineSegment(sketch, "E23.2", {"start": v(62, -57.5) * mm, "end": v(59.4, -53.09) * mm});
            skLineSegment(sketch, "E23.3", {"start": v(59.4, -53.09) * mm, "end": v(61.93, -48.64) * mm});
            skLineSegment(sketch, "E23.4", {"start": v(61.93, -48.64) * mm, "end": v(67.04, -48.6) * mm});
            skLineSegment(sketch, "E23.5", {"start": v(67.04, -48.6) * mm, "end": v(69.63, -53.01) * mm});
            skPoint(sketch, "E23.0.midPoint", {"position": v(68.37, -55.23) * mm});
            skSolve(sketch);
        }
        {
            var Q0;
            Q0 = qSketchRegion(id + "F3", true);
            extrude(context, id + "F4", {"entities" : qUnion([Q0]), "operationType" : NewBodyOperationType.ADD, "depth" : 25 * mm, "offsetDistance" : 25 * mm});
        }
        {
            var Q0;
            Q0=makeQuery(id+"F4.opExtrude","CAP_FACE",FACE,{"disambiguationData":[OSD([sQuery(id+"F3.wireOp",EDGE,"E17.0"),sQuery(id+"F3.wireOp",EDGE,"E17.1"),sQuery(id+"F3.wireOp",EDGE,"E17.2"),sQuery(id+"F3.wireOp",EDGE,"E17.3"),sQuery(id+"F3.wireOp",EDGE,"E17.4"),sQuery(id+"F3.wireOp",EDGE,"E17.5"),sQuery(id+"F3.wireOp",EDGE,"E17.6"),sQuery(id+"F3.wireOp",EDGE,"E17.7")])],"isStart":false});
            var sketch = newSketch(context, id + "F5", { "sketchPlane" : qUnion([Q0])});
            skLineSegment(sketch, "E24.bottom", {"start": v(-235.63, 107.32) * mm, "end": v(70.34, 107.32) * mm});
            skLineSegment(sketch, "E24.top", {"start": v(-235.63, -131.2) * mm, "end": v(70.34, -131.2) * mm});
            skLineSegment(sketch, "E24.left", {"start": v(-235.63, 107.32) * mm, "end": v(-235.63, -131.2) * mm});
            skLineSegment(sketch, "E24.right", {"start": v(70.34, 107.32) * mm, "end": v(70.34, -131.2) * mm});
            skCircle(sketch, "E25", {"center": v(-92.84, 103.15) * mm, "radius": 1.85 * mm});
            skCircle(sketch, "E26", {"center": v(-92.84, -65.99) * mm, "radius": 1.85 * mm});
            skCircle(sketch, "E27", {"center": v(-220.11, -122.97) * mm, "radius": 1.51 * mm});
            skCircle(sketch, "E28", {"center": v(-217.23, 103.11) * mm, "radius": 1.53 * mm});
            skCircle(sketch, "E29", {"center": v(64.69, -122.94) * mm, "radius": 1.55 * mm});
            skCircle(sketch, "E30", {"center": v(64.69, -52.95) * mm, "radius": 1.59 * mm});
            skCircle(sketch, "E31", {"center": v(64.68, 79.07) * mm, "radius": 1.52 * mm});
            skSolve(sketch);
        }
        {
            var Q0;
            Q0 = qSketchRegion(id + "F5", true);
            extrude(context, id + "F6", {"entities" : qUnion([Q0]), "operationType" : NewBodyOperationType.ADD, "depth" : 2 * mm, "offsetDistance" : 25 * mm});
        }
        {
            var Q0;
            Q0=makeQuery(id+"F6.opExtrude","CAP_FACE",FACE,{"disambiguationData":[OSD([sQuery(id+"F5.wireOp",EDGE,"E24.bottom"),sQuery(id+"F5.wireOp",EDGE,"E24.top"),sQuery(id+"F5.wireOp",EDGE,"E24.left"),sQuery(id+"F5.wireOp",EDGE,"E24.right"),sQuery(id+"F5.wireOp",EDGE,"E25"),sQuery(id+"F5.wireOp",EDGE,"E26"),sQuery(id+"F5.wireOp",EDGE,"E27"),sQuery(id+"F5.wireOp",EDGE,"E28"),sQuery(id+"F5.wireOp",EDGE,"E29"),sQuery(id+"F5.wireOp",EDGE,"E30"),sQuery(id+"F5.wireOp",EDGE,"E31")])],"isStart":false});
            var sketch = newSketch(context, id + "F7", { "sketchPlane" : qUnion([Q0])});
            skLineSegment(sketch, "E32", {"start": v(70.34, 107.32) * mm, "end": v(70.34, 94.19) * mm});
            skLineSegment(sketch, "E33", {"start": v(70.34, 94.19) * mm, "end": v(57.19, 75.01) * mm});
            skLineSegment(sketch, "E34", {"start": v(57.19, 75.01) * mm, "end": v(-17.77, 47.32) * mm});
            skLineSegment(sketch, "E35", {"start": v(-17.77, 47.32) * mm, "end": v(-79.1, 72.54) * mm});
            skLineSegment(sketch, "E36", {"start": v(-79.1, 72.54) * mm, "end": v(-89.66, 107.32) * mm});
            skLineSegment(sketch, "E37", {"start": v(-89.66, 107.32) * mm, "end": v(70.34, 107.32) * mm});
            skLineSegment(sketch, "E38", {"start": v(-89.66, 107.32) * mm, "end": v(-89.66, 72.75) * mm});
            skLineSegment(sketch, "E39", {"start": v(-89.66, 72.75) * mm, "end": v(-79.1, 72.54) * mm});
            skLineSegment(sketch, "E40.bottom", {"start": v(-101.38, 103.86) * mm, "end": v(-111.72, 103.86) * mm});
            skLineSegment(sketch, "E40.top", {"start": v(-101.38, -7.75) * mm, "end": v(-111.72, -7.75) * mm});
            skLineSegment(sketch, "E40.left", {"start": v(-101.38, 103.86) * mm, "end": v(-101.38, -7.75) * mm});
            skLineSegment(sketch, "E40.right", {"start": v(-111.72, 103.86) * mm, "end": v(-111.72, -7.75) * mm});
            skLineSegment(sketch, "E41.bottom", {"start": v(-134.22, 103.83) * mm, "end": v(-144.22, 103.83) * mm});
            skLineSegment(sketch, "E41.top", {"start": v(-134.22, -7.75) * mm, "end": v(-144.22, -7.75) * mm});
            skLineSegment(sketch, "E41.left", {"start": v(-134.22, 103.83) * mm, "end": v(-134.22, -7.75) * mm});
            skLineSegment(sketch, "E41.right", {"start": v(-144.22, 103.83) * mm, "end": v(-144.22, -7.75) * mm});
            skLineSegment(sketch, "E42.bottom", {"start": v(-165.84, 103.83) * mm, "end": v(-175.83, 103.83) * mm});
            skLineSegment(sketch, "E42.top", {"start": v(-165.84, -7.9) * mm, "end": v(-175.83, -7.9) * mm});
            skLineSegment(sketch, "E42.left", {"start": v(-165.84, 103.83) * mm, "end": v(-165.84, -7.9) * mm});
            skLineSegment(sketch, "E42.right", {"start": v(-175.83, 103.83) * mm, "end": v(-175.83, -7.9) * mm});
            skLineSegment(sketch, "E43.bottom", {"start": v(18.88, 24.08) * mm, "end": v(-46.12, 24.08) * mm});
            skLineSegment(sketch, "E43.top", {"start": v(18.88, -40.92) * mm, "end": v(-46.12, -40.92) * mm});
            skLineSegment(sketch, "E43.left", {"start": v(18.88, 24.08) * mm, "end": v(18.88, -40.92) * mm});
            skLineSegment(sketch, "E43.right", {"start": v(-46.12, 24.08) * mm, "end": v(-46.12, -40.92) * mm});
            skLineSegment(sketch, "E44.bottom", {"start": v(36.21, -97.39) * mm, "end": v(-91.04, -97.39) * mm});
            skLineSegment(sketch, "E44.top", {"start": v(36.21, -106.37) * mm, "end": v(-91.04, -106.37) * mm});
            skLineSegment(sketch, "E44.left", {"start": v(36.21, -97.39) * mm, "end": v(36.21, -106.37) * mm});
            skLineSegment(sketch, "E44.right", {"start": v(-91.04, -97.39) * mm, "end": v(-91.04, -106.37) * mm});
            skLineSegment(sketch, "E45.bottom", {"start": v(36.21, -85.81) * mm, "end": v(-91.04, -85.81) * mm});
            skLineSegment(sketch, "E45.top", {"start": v(36.21, -94.79) * mm, "end": v(-91.04, -94.79) * mm});
            skLineSegment(sketch, "E45.left", {"start": v(36.21, -85.81) * mm, "end": v(36.21, -94.79) * mm});
            skLineSegment(sketch, "E45.right", {"start": v(-91.04, -85.81) * mm, "end": v(-91.04, -94.79) * mm});
            skLineSegment(sketch, "E46.bottom", {"start": v(36.21, -74.23) * mm, "end": v(-91.04, -74.23) * mm});
            skLineSegment(sketch, "E46.top", {"start": v(36.21, -83.21) * mm, "end": v(-91.04, -83.21) * mm});
            skLineSegment(sketch, "E46.left", {"start": v(36.21, -74.23) * mm, "end": v(36.21, -83.21) * mm});
            skLineSegment(sketch, "E46.right", {"start": v(-91.04, -74.23) * mm, "end": v(-91.04, -83.21) * mm});
            skLineSegment(sketch, "E47.bottom", {"start": v(36.21, -62.66) * mm, "end": v(-91.04, -62.66) * mm});
            skLineSegment(sketch, "E47.top", {"start": v(36.21, -71.63) * mm, "end": v(-91.04, -71.63) * mm});
            skLineSegment(sketch, "E47.left", {"start": v(36.21, -62.66) * mm, "end": v(36.21, -71.63) * mm});
            skLineSegment(sketch, "E47.right", {"start": v(-91.04, -62.66) * mm, "end": v(-91.04, -71.63) * mm});
            skSolve(sketch);
        }
        {
            var Q0;
            Q0=makeQuery(id+"F7.imprint","IMPRINT",FACE,{"disambiguationData":[TD([[makeQuery(id+"F7.imprint","IMPRINT",EDGE,{"derivedFrom":sQuery(id+"F7.wireOp",EDGE,"E32")}),-1.0]])]});
            extrude(context, id + "F8", {"entities" : qUnion([Q0]), "operationType" : NewBodyOperationType.ADD, "depth" : 46 * mm, "offsetDistance" : 25 * mm});
        }
        {
            var Q0;
            Q0=makeQuery(id+"F1.opExtrude","CAP_FACE",FACE,{"disambiguationData":[OSD([sQuery(id+"F0.wireOp",EDGE,"E0.bottom"),sQuery(id+"F0.wireOp",EDGE,"E0.top"),sQuery(id+"F0.wireOp",EDGE,"E0.left"),sQuery(id+"F0.wireOp",EDGE,"E0.right"),sQuery(id+"F0.wireOp",EDGE,"E2.bottom"),sQuery(id+"F0.wireOp",EDGE,"E2.top"),sQuery(id+"F0.wireOp",EDGE,"E2.left"),sQuery(id+"F0.wireOp",EDGE,"E2.right"),sQuery(id+"F0.wireOp",EDGE,"iKlQyD2N-WRxG-utMa-lJ8L-cIOPaJfjkMKQ"),sQuery(id+"F0.wireOp",EDGE,"8L1Znl8v-4MLT-wmsx-H5cy-UTvKXKrOukI6"),sQuery(id+"F0.wireOp",EDGE,"fnGGJgAr-T0BG-MF3t-gyGZ-hbNT0MP3fvNB"),sQuery(id+"F0.wireOp",EDGE,"E3"),sQuery(id+"F0.wireOp",EDGE,"E4"),sQuery(id+"F0.wireOp",EDGE,"E5"),sQuery(id+"F0.wireOp",EDGE,"E6"),sQuery(id+"F0.wireOp",EDGE,"E7"),sQuery(id+"F0.wireOp",EDGE,"E8"),sQuery(id+"F0.wireOp",EDGE,"E9"),sQuery(id+"F0.wireOp",EDGE,"ib4XqY8O-GvjW-DCsm-aGK6-8DvLvJzzPkUd"),sQuery(id+"F0.wireOp",EDGE,"BiZwc9jZ-H7PX-ENaB-XFIt-c00jdd6Leh9H")])],"isStart":false});
            var sketch = newSketch(context, id + "F9", { "sketchPlane" : qUnion([Q0])});
            skLineSegment(sketch, "E48.bottom", {"start": v(78.88, -86.6) * mm, "end": v(165.17, -86.6) * mm});
            skLineSegment(sketch, "E48.top", {"start": v(78.88, 70.02) * mm, "end": v(165.17, 70.02) * mm});
            skLineSegment(sketch, "E48.left", {"start": v(78.88, -86.6) * mm, "end": v(78.88, 70.02) * mm});
            skLineSegment(sketch, "E48.right", {"start": v(165.17, -86.6) * mm, "end": v(165.17, 70.02) * mm});
            skSolve(sketch);
        }
        {
            var Q0;
            Q0 = qSketchRegion(id + "F9", true);
            extrude(context, id + "F10", {"entities" : qUnion([Q0]), "operationType" : NewBodyOperationType.ADD, "depth" : 185 * mm, "offsetDistance" : 25 * mm});
        }
        {
            var Q0;
            Q0=makeQuery(id+"F10.opExtrude","CAP_FACE",FACE,{"disambiguationData":[OSD([sQuery(id+"F9.wireOp",EDGE,"E48.bottom"),sQuery(id+"F9.wireOp",EDGE,"E48.top"),sQuery(id+"F9.wireOp",EDGE,"E48.left"),sQuery(id+"F9.wireOp",EDGE,"E48.right")])],"isStart":false});
            var sketch = newSketch(context, id + "F11", { "sketchPlane" : qUnion([Q0])});
            skCircle(sketch, "E49", {"center": v(119.8, -58.71) * mm, "radius": 19.44 * mm});
            skLineSegment(sketch, "E50.bottom", {"start": v(129.93, -22.61) * mm, "end": v(149.93, -22.61) * mm});
            skLineSegment(sketch, "E50.top", {"start": v(129.93, -2.61) * mm, "end": v(149.93, -2.61) * mm});
            skLineSegment(sketch, "E50.left", {"start": v(129.93, -22.61) * mm, "end": v(129.93, -2.61) * mm});
            skLineSegment(sketch, "E50.right", {"start": v(149.93, -22.61) * mm, "end": v(149.93, -2.61) * mm});
            skLineSegment(sketch, "E51.bottom", {"start": v(143.54, -22.06) * mm, "end": v(149.14, -22.06) * mm});
            skLineSegment(sketch, "E51.top", {"start": v(143.54, -16.46) * mm, "end": v(149.14, -16.46) * mm});
            skLineSegment(sketch, "E51.left", {"start": v(143.54, -22.06) * mm, "end": v(143.54, -16.46) * mm});
            skLineSegment(sketch, "E51.right", {"start": v(149.14, -22.06) * mm, "end": v(149.14, -16.46) * mm});
            skLineSegment(sketch, "E52.bottom", {"start": v(143.54, -15.75) * mm, "end": v(149.19, -15.75) * mm});
            skLineSegment(sketch, "E52.top", {"start": v(143.54, -10.11) * mm, "end": v(149.19, -10.11) * mm});
            skLineSegment(sketch, "E52.left", {"start": v(143.54, -15.75) * mm, "end": v(143.54, -10.11) * mm});
            skLineSegment(sketch, "E52.right", {"start": v(149.19, -15.75) * mm, "end": v(149.19, -10.11) * mm});
            skLineSegment(sketch, "E53.bottom", {"start": v(143.54, -9.25) * mm, "end": v(149.19, -9.25) * mm});
            skLineSegment(sketch, "E53.top", {"start": v(143.54, -3.64) * mm, "end": v(149.19, -3.64) * mm});
            skLineSegment(sketch, "E53.left", {"start": v(143.54, -9.25) * mm, "end": v(143.54, -3.64) * mm});
            skLineSegment(sketch, "E53.right", {"start": v(149.19, -9.25) * mm, "end": v(149.19, -3.64) * mm});
            skLineSegment(sketch, "E54.bottom", {"start": v(142.9, -16.46) * mm, "end": v(137.24, -16.46) * mm});
            skLineSegment(sketch, "E54.top", {"start": v(142.9, -22.09) * mm, "end": v(137.24, -22.09) * mm});
            skLineSegment(sketch, "E54.left", {"start": v(142.9, -16.46) * mm, "end": v(142.9, -22.09) * mm});
            skLineSegment(sketch, "E54.right", {"start": v(137.24, -16.46) * mm, "end": v(137.24, -22.09) * mm});
            skLineSegment(sketch, "E55.bottom", {"start": v(142.9, -15.75) * mm, "end": v(137.23, -15.75) * mm});
            skLineSegment(sketch, "E55.top", {"start": v(142.9, -10.11) * mm, "end": v(137.23, -10.11) * mm});
            skLineSegment(sketch, "E55.left", {"start": v(142.9, -15.75) * mm, "end": v(142.9, -10.11) * mm});
            skLineSegment(sketch, "E55.right", {"start": v(137.23, -15.75) * mm, "end": v(137.23, -10.11) * mm});
            skLineSegment(sketch, "E56.bottom", {"start": v(142.9, -9.25) * mm, "end": v(137.23, -9.25) * mm});
            skLineSegment(sketch, "E56.top", {"start": v(142.9, -3.64) * mm, "end": v(137.23, -3.64) * mm});
            skLineSegment(sketch, "E56.left", {"start": v(142.9, -9.25) * mm, "end": v(142.9, -3.64) * mm});
            skLineSegment(sketch, "E56.right", {"start": v(137.23, -9.25) * mm, "end": v(137.23, -3.64) * mm});
            skLineSegment(sketch, "E57.bottom", {"start": v(136.58, -22.09) * mm, "end": v(130.77, -22.09) * mm});
            skLineSegment(sketch, "E57.top", {"start": v(136.58, -16.46) * mm, "end": v(130.77, -16.46) * mm});
            skLineSegment(sketch, "E57.left", {"start": v(136.58, -22.09) * mm, "end": v(136.58, -16.46) * mm});
            skLineSegment(sketch, "E57.right", {"start": v(130.77, -22.09) * mm, "end": v(130.77, -16.46) * mm});
            skLineSegment(sketch, "E58.bottom", {"start": v(136.58, -15.75) * mm, "end": v(130.77, -15.75) * mm});
            skLineSegment(sketch, "E58.top", {"start": v(136.58, -10.11) * mm, "end": v(130.77, -10.11) * mm});
            skLineSegment(sketch, "E58.left", {"start": v(136.58, -15.75) * mm, "end": v(136.58, -10.11) * mm});
            skLineSegment(sketch, "E58.right", {"start": v(130.77, -15.75) * mm, "end": v(130.77, -10.11) * mm});
            skLineSegment(sketch, "E59.bottom", {"start": v(136.58, -9.25) * mm, "end": v(130.77, -9.25) * mm});
            skLineSegment(sketch, "E59.top", {"start": v(136.58, -3.64) * mm, "end": v(130.77, -3.64) * mm});
            skLineSegment(sketch, "E59.left", {"start": v(136.58, -9.25) * mm, "end": v(136.58, -3.64) * mm});
            skLineSegment(sketch, "E59.right", {"start": v(130.77, -9.25) * mm, "end": v(130.77, -3.64) * mm});
            skCircle(sketch, "E60", {"center": v(119.8, -58.71) * mm, "radius": 18.16 * mm});
            skLineSegment(sketch, "E61.bottom", {"start": v(129.93, 9.02) * mm, "end": v(149.93, 9.02) * mm});
            skLineSegment(sketch, "E61.top", {"start": v(129.93, 29.02) * mm, "end": v(149.93, 29.02) * mm});
            skLineSegment(sketch, "E61.left", {"start": v(129.93, 9.02) * mm, "end": v(129.93, 29.02) * mm});
            skLineSegment(sketch, "E61.right", {"start": v(149.93, 9.02) * mm, "end": v(149.93, 29.02) * mm});
            skLineSegment(sketch, "E62.bottom", {"start": v(143.54, 9.57) * mm, "end": v(149.14, 9.57) * mm});
            skLineSegment(sketch, "E62.top", {"start": v(143.54, 15.17) * mm, "end": v(149.14, 15.17) * mm});
            skLineSegment(sketch, "E62.left", {"start": v(143.54, 9.57) * mm, "end": v(143.54, 15.17) * mm});
            skLineSegment(sketch, "E62.right", {"start": v(149.14, 9.57) * mm, "end": v(149.14, 15.17) * mm});
            skLineSegment(sketch, "E63.bottom", {"start": v(143.54, 15.88) * mm, "end": v(149.19, 15.88) * mm});
            skLineSegment(sketch, "E63.top", {"start": v(143.54, 21.52) * mm, "end": v(149.19, 21.52) * mm});
            skLineSegment(sketch, "E63.left", {"start": v(143.54, 15.88) * mm, "end": v(143.54, 21.52) * mm});
            skLineSegment(sketch, "E63.right", {"start": v(149.19, 15.88) * mm, "end": v(149.19, 21.52) * mm});
            skLineSegment(sketch, "E64.bottom", {"start": v(143.54, 22.38) * mm, "end": v(149.19, 22.38) * mm});
            skLineSegment(sketch, "E64.top", {"start": v(143.54, 28) * mm, "end": v(149.19, 28) * mm});
            skLineSegment(sketch, "E64.left", {"start": v(143.54, 22.38) * mm, "end": v(143.54, 28) * mm});
            skLineSegment(sketch, "E64.right", {"start": v(149.19, 22.38) * mm, "end": v(149.19, 28) * mm});
            skLineSegment(sketch, "E65.bottom", {"start": v(142.9, 15.17) * mm, "end": v(137.24, 15.17) * mm});
            skLineSegment(sketch, "E65.top", {"start": v(142.9, 9.54) * mm, "end": v(137.24, 9.54) * mm});
            skLineSegment(sketch, "E65.left", {"start": v(142.9, 15.17) * mm, "end": v(142.9, 9.54) * mm});
            skLineSegment(sketch, "E65.right", {"start": v(137.24, 15.17) * mm, "end": v(137.24, 9.54) * mm});
            skLineSegment(sketch, "E66.bottom", {"start": v(142.9, 15.88) * mm, "end": v(137.23, 15.88) * mm});
            skLineSegment(sketch, "E66.top", {"start": v(142.9, 21.52) * mm, "end": v(137.23, 21.52) * mm});
            skLineSegment(sketch, "E66.left", {"start": v(142.9, 15.88) * mm, "end": v(142.9, 21.52) * mm});
            skLineSegment(sketch, "E66.right", {"start": v(137.23, 15.88) * mm, "end": v(137.23, 21.52) * mm});
            skLineSegment(sketch, "E67.bottom", {"start": v(142.9, 22.38) * mm, "end": v(137.23, 22.38) * mm});
            skLineSegment(sketch, "E67.top", {"start": v(142.9, 28) * mm, "end": v(137.23, 28) * mm});
            skLineSegment(sketch, "E67.left", {"start": v(142.9, 22.38) * mm, "end": v(142.9, 28) * mm});
            skLineSegment(sketch, "E67.right", {"start": v(137.23, 22.38) * mm, "end": v(137.23, 28) * mm});
            skLineSegment(sketch, "E68.bottom", {"start": v(136.58, 9.54) * mm, "end": v(130.77, 9.54) * mm});
            skLineSegment(sketch, "E68.top", {"start": v(136.58, 15.17) * mm, "end": v(130.77, 15.17) * mm});
            skLineSegment(sketch, "E68.left", {"start": v(136.58, 9.54) * mm, "end": v(136.58, 15.17) * mm});
            skLineSegment(sketch, "E68.right", {"start": v(130.77, 9.54) * mm, "end": v(130.77, 15.17) * mm});
            skLineSegment(sketch, "E69.bottom", {"start": v(136.58, 15.88) * mm, "end": v(130.77, 15.88) * mm});
            skLineSegment(sketch, "E69.top", {"start": v(136.58, 21.52) * mm, "end": v(130.77, 21.52) * mm});
            skLineSegment(sketch, "E69.left", {"start": v(136.58, 15.88) * mm, "end": v(136.58, 21.52) * mm});
            skLineSegment(sketch, "E69.right", {"start": v(130.77, 15.88) * mm, "end": v(130.77, 21.52) * mm});
            skLineSegment(sketch, "E70.bottom", {"start": v(136.58, 22.38) * mm, "end": v(130.77, 22.38) * mm});
            skLineSegment(sketch, "E70.top", {"start": v(136.58, 28) * mm, "end": v(130.77, 28) * mm});
            skLineSegment(sketch, "E70.left", {"start": v(136.58, 22.38) * mm, "end": v(136.58, 28) * mm});
            skLineSegment(sketch, "E70.right", {"start": v(130.77, 22.38) * mm, "end": v(130.77, 28) * mm});
            skLineSegment(sketch, "E71.bottom", {"start": v(129.93, 39.12) * mm, "end": v(149.93, 39.12) * mm});
            skLineSegment(sketch, "E71.top", {"start": v(129.93, 59.12) * mm, "end": v(149.93, 59.12) * mm});
            skLineSegment(sketch, "E71.left", {"start": v(129.93, 39.12) * mm, "end": v(129.93, 59.12) * mm});
            skLineSegment(sketch, "E71.right", {"start": v(149.93, 39.12) * mm, "end": v(149.93, 59.12) * mm});
            skLineSegment(sketch, "E72.bottom", {"start": v(143.54, 39.67) * mm, "end": v(149.14, 39.67) * mm});
            skLineSegment(sketch, "E72.top", {"start": v(143.54, 45.27) * mm, "end": v(149.14, 45.27) * mm});
            skLineSegment(sketch, "E72.left", {"start": v(143.54, 39.67) * mm, "end": v(143.54, 45.27) * mm});
            skLineSegment(sketch, "E72.right", {"start": v(149.14, 39.67) * mm, "end": v(149.14, 45.27) * mm});
            skLineSegment(sketch, "E73.bottom", {"start": v(143.54, 45.98) * mm, "end": v(149.19, 45.98) * mm});
            skLineSegment(sketch, "E73.top", {"start": v(143.54, 51.62) * mm, "end": v(149.19, 51.62) * mm});
            skLineSegment(sketch, "E73.left", {"start": v(143.54, 45.98) * mm, "end": v(143.54, 51.62) * mm});
            skLineSegment(sketch, "E73.right", {"start": v(149.19, 45.98) * mm, "end": v(149.19, 51.62) * mm});
            skLineSegment(sketch, "E74.bottom", {"start": v(143.54, 52.48) * mm, "end": v(149.19, 52.48) * mm});
            skLineSegment(sketch, "E74.top", {"start": v(143.54, 58.1) * mm, "end": v(149.19, 58.1) * mm});
            skLineSegment(sketch, "E74.left", {"start": v(143.54, 52.48) * mm, "end": v(143.54, 58.1) * mm});
            skLineSegment(sketch, "E74.right", {"start": v(149.19, 52.48) * mm, "end": v(149.19, 58.1) * mm});
            skLineSegment(sketch, "E75.bottom", {"start": v(142.9, 45.27) * mm, "end": v(137.24, 45.27) * mm});
            skLineSegment(sketch, "E75.top", {"start": v(142.9, 39.64) * mm, "end": v(137.24, 39.64) * mm});
            skLineSegment(sketch, "E75.left", {"start": v(142.9, 45.27) * mm, "end": v(142.9, 39.64) * mm});
            skLineSegment(sketch, "E75.right", {"start": v(137.24, 45.27) * mm, "end": v(137.24, 39.64) * mm});
            skLineSegment(sketch, "E76.bottom", {"start": v(142.9, 45.98) * mm, "end": v(137.23, 45.98) * mm});
            skLineSegment(sketch, "E76.top", {"start": v(142.9, 51.62) * mm, "end": v(137.23, 51.62) * mm});
            skLineSegment(sketch, "E76.left", {"start": v(142.9, 45.98) * mm, "end": v(142.9, 51.62) * mm});
            skLineSegment(sketch, "E76.right", {"start": v(137.23, 45.98) * mm, "end": v(137.23, 51.62) * mm});
            skLineSegment(sketch, "E77.bottom", {"start": v(142.9, 52.48) * mm, "end": v(137.23, 52.48) * mm});
            skLineSegment(sketch, "E77.top", {"start": v(142.9, 58.1) * mm, "end": v(137.23, 58.1) * mm});
            skLineSegment(sketch, "E77.left", {"start": v(142.9, 52.48) * mm, "end": v(142.9, 58.1) * mm});
            skLineSegment(sketch, "E77.right", {"start": v(137.23, 52.48) * mm, "end": v(137.23, 58.1) * mm});
            skLineSegment(sketch, "E78.bottom", {"start": v(136.58, 39.64) * mm, "end": v(130.77, 39.64) * mm});
            skLineSegment(sketch, "E78.top", {"start": v(136.58, 45.27) * mm, "end": v(130.77, 45.27) * mm});
            skLineSegment(sketch, "E78.left", {"start": v(136.58, 39.64) * mm, "end": v(136.58, 45.27) * mm});
            skLineSegment(sketch, "E78.right", {"start": v(130.77, 39.64) * mm, "end": v(130.77, 45.27) * mm});
            skLineSegment(sketch, "E79.bottom", {"start": v(136.58, 45.98) * mm, "end": v(130.77, 45.98) * mm});
            skLineSegment(sketch, "E79.top", {"start": v(136.58, 51.62) * mm, "end": v(130.77, 51.62) * mm});
            skLineSegment(sketch, "E79.left", {"start": v(136.58, 45.98) * mm, "end": v(136.58, 51.62) * mm});
            skLineSegment(sketch, "E79.right", {"start": v(130.77, 45.98) * mm, "end": v(130.77, 51.62) * mm});
            skLineSegment(sketch, "E80.bottom", {"start": v(136.58, 52.48) * mm, "end": v(130.77, 52.48) * mm});
            skLineSegment(sketch, "E80.top", {"start": v(136.58, 58.1) * mm, "end": v(130.77, 58.1) * mm});
            skLineSegment(sketch, "E80.left", {"start": v(136.58, 52.48) * mm, "end": v(136.58, 58.1) * mm});
            skLineSegment(sketch, "E80.right", {"start": v(130.77, 52.48) * mm, "end": v(130.77, 58.1) * mm});
            skLineSegment(sketch, "E81.bottom", {"start": v(93.38, -22.61) * mm, "end": v(113.38, -22.61) * mm});
            skLineSegment(sketch, "E81.top", {"start": v(93.38, -2.61) * mm, "end": v(113.38, -2.61) * mm});
            skLineSegment(sketch, "E81.left", {"start": v(93.38, -22.61) * mm, "end": v(93.38, -2.61) * mm});
            skLineSegment(sketch, "E81.right", {"start": v(113.38, -22.61) * mm, "end": v(113.38, -2.61) * mm});
            skLineSegment(sketch, "E82.bottom", {"start": v(106.99, -22.06) * mm, "end": v(112.59, -22.06) * mm});
            skLineSegment(sketch, "E82.top", {"start": v(106.99, -16.46) * mm, "end": v(112.59, -16.46) * mm});
            skLineSegment(sketch, "E82.left", {"start": v(106.99, -22.06) * mm, "end": v(106.99, -16.46) * mm});
            skLineSegment(sketch, "E82.right", {"start": v(112.59, -22.06) * mm, "end": v(112.59, -16.46) * mm});
            skLineSegment(sketch, "E83.bottom", {"start": v(106.99, -15.75) * mm, "end": v(112.63, -15.75) * mm});
            skLineSegment(sketch, "E83.top", {"start": v(106.99, -10.11) * mm, "end": v(112.63, -10.11) * mm});
            skLineSegment(sketch, "E83.left", {"start": v(106.99, -15.75) * mm, "end": v(106.99, -10.11) * mm});
            skLineSegment(sketch, "E83.right", {"start": v(112.63, -15.75) * mm, "end": v(112.63, -10.11) * mm});
            skLineSegment(sketch, "E84.bottom", {"start": v(106.99, -9.25) * mm, "end": v(112.63, -9.25) * mm});
            skLineSegment(sketch, "E84.top", {"start": v(106.99, -3.64) * mm, "end": v(112.63, -3.64) * mm});
            skLineSegment(sketch, "E84.left", {"start": v(106.99, -9.25) * mm, "end": v(106.99, -3.64) * mm});
            skLineSegment(sketch, "E84.right", {"start": v(112.63, -9.25) * mm, "end": v(112.63, -3.64) * mm});
            skLineSegment(sketch, "E85.bottom", {"start": v(106.35, -16.46) * mm, "end": v(100.68, -16.46) * mm});
            skLineSegment(sketch, "E85.top", {"start": v(106.35, -22.09) * mm, "end": v(100.68, -22.09) * mm});
            skLineSegment(sketch, "E85.left", {"start": v(106.35, -16.46) * mm, "end": v(106.35, -22.09) * mm});
            skLineSegment(sketch, "E85.right", {"start": v(100.68, -16.46) * mm, "end": v(100.68, -22.09) * mm});
            skLineSegment(sketch, "E86.bottom", {"start": v(106.35, -15.75) * mm, "end": v(100.68, -15.75) * mm});
            skLineSegment(sketch, "E86.top", {"start": v(106.35, -10.11) * mm, "end": v(100.68, -10.11) * mm});
            skLineSegment(sketch, "E86.left", {"start": v(106.35, -15.75) * mm, "end": v(106.35, -10.11) * mm});
            skLineSegment(sketch, "E86.right", {"start": v(100.68, -15.75) * mm, "end": v(100.68, -10.11) * mm});
            skLineSegment(sketch, "E87.bottom", {"start": v(106.35, -9.25) * mm, "end": v(100.68, -9.25) * mm});
            skLineSegment(sketch, "E87.top", {"start": v(106.35, -3.64) * mm, "end": v(100.68, -3.64) * mm});
            skLineSegment(sketch, "E87.left", {"start": v(106.35, -9.25) * mm, "end": v(106.35, -3.64) * mm});
            skLineSegment(sketch, "E87.right", {"start": v(100.68, -9.25) * mm, "end": v(100.68, -3.64) * mm});
            skLineSegment(sketch, "E88.bottom", {"start": v(100.02, -22.09) * mm, "end": v(94.21, -22.09) * mm});
            skLineSegment(sketch, "E88.top", {"start": v(100.02, -16.46) * mm, "end": v(94.21, -16.46) * mm});
            skLineSegment(sketch, "E88.left", {"start": v(100.02, -22.09) * mm, "end": v(100.02, -16.46) * mm});
            skLineSegment(sketch, "E88.right", {"start": v(94.21, -22.09) * mm, "end": v(94.21, -16.46) * mm});
            skLineSegment(sketch, "E89.bottom", {"start": v(100.02, -15.75) * mm, "end": v(94.21, -15.75) * mm});
            skLineSegment(sketch, "E89.top", {"start": v(100.02, -10.11) * mm, "end": v(94.21, -10.11) * mm});
            skLineSegment(sketch, "E89.left", {"start": v(100.02, -15.75) * mm, "end": v(100.02, -10.11) * mm});
            skLineSegment(sketch, "E89.right", {"start": v(94.21, -15.75) * mm, "end": v(94.21, -10.11) * mm});
            skLineSegment(sketch, "E90.bottom", {"start": v(100.02, -9.25) * mm, "end": v(94.21, -9.25) * mm});
            skLineSegment(sketch, "E90.top", {"start": v(100.02, -3.64) * mm, "end": v(94.21, -3.64) * mm});
            skLineSegment(sketch, "E90.left", {"start": v(100.02, -9.25) * mm, "end": v(100.02, -3.64) * mm});
            skLineSegment(sketch, "E90.right", {"start": v(94.21, -9.25) * mm, "end": v(94.21, -3.64) * mm});
            skLineSegment(sketch, "E91.bottom", {"start": v(93.38, 8.2) * mm, "end": v(113.38, 8.2) * mm});
            skLineSegment(sketch, "E91.top", {"start": v(93.38, 28.2) * mm, "end": v(113.38, 28.2) * mm});
            skLineSegment(sketch, "E91.left", {"start": v(93.38, 8.2) * mm, "end": v(93.38, 28.2) * mm});
            skLineSegment(sketch, "E91.right", {"start": v(113.38, 8.2) * mm, "end": v(113.38, 28.2) * mm});
            skLineSegment(sketch, "E92.bottom", {"start": v(106.99, 8.75) * mm, "end": v(112.59, 8.75) * mm});
            skLineSegment(sketch, "E92.top", {"start": v(106.99, 14.35) * mm, "end": v(112.59, 14.35) * mm});
            skLineSegment(sketch, "E92.left", {"start": v(106.99, 8.75) * mm, "end": v(106.99, 14.35) * mm});
            skLineSegment(sketch, "E92.right", {"start": v(112.59, 8.75) * mm, "end": v(112.59, 14.35) * mm});
            skLineSegment(sketch, "E93.bottom", {"start": v(106.99, 15.06) * mm, "end": v(112.63, 15.06) * mm});
            skLineSegment(sketch, "E93.top", {"start": v(106.99, 20.7) * mm, "end": v(112.63, 20.7) * mm});
            skLineSegment(sketch, "E93.left", {"start": v(106.99, 15.06) * mm, "end": v(106.99, 20.7) * mm});
            skLineSegment(sketch, "E93.right", {"start": v(112.63, 15.06) * mm, "end": v(112.63, 20.7) * mm});
            skLineSegment(sketch, "E94.bottom", {"start": v(106.99, 21.56) * mm, "end": v(112.63, 21.56) * mm});
            skLineSegment(sketch, "E94.top", {"start": v(106.99, 27.17) * mm, "end": v(112.63, 27.17) * mm});
            skLineSegment(sketch, "E94.left", {"start": v(106.99, 21.56) * mm, "end": v(106.99, 27.17) * mm});
            skLineSegment(sketch, "E94.right", {"start": v(112.63, 21.56) * mm, "end": v(112.63, 27.17) * mm});
            skLineSegment(sketch, "E95.bottom", {"start": v(106.35, 14.35) * mm, "end": v(100.68, 14.35) * mm});
            skLineSegment(sketch, "E95.top", {"start": v(106.35, 8.72) * mm, "end": v(100.68, 8.72) * mm});
            skLineSegment(sketch, "E95.left", {"start": v(106.35, 14.35) * mm, "end": v(106.35, 8.72) * mm});
            skLineSegment(sketch, "E95.right", {"start": v(100.68, 14.35) * mm, "end": v(100.68, 8.72) * mm});
            skLineSegment(sketch, "E96.bottom", {"start": v(106.35, 15.06) * mm, "end": v(100.68, 15.06) * mm});
            skLineSegment(sketch, "E96.top", {"start": v(106.35, 20.7) * mm, "end": v(100.68, 20.7) * mm});
            skLineSegment(sketch, "E96.left", {"start": v(106.35, 15.06) * mm, "end": v(106.35, 20.7) * mm});
            skLineSegment(sketch, "E96.right", {"start": v(100.68, 15.06) * mm, "end": v(100.68, 20.7) * mm});
            skLineSegment(sketch, "E97.bottom", {"start": v(106.35, 21.56) * mm, "end": v(100.68, 21.56) * mm});
            skLineSegment(sketch, "E97.top", {"start": v(106.35, 27.17) * mm, "end": v(100.68, 27.17) * mm});
            skLineSegment(sketch, "E97.left", {"start": v(106.35, 21.56) * mm, "end": v(106.35, 27.17) * mm});
            skLineSegment(sketch, "E97.right", {"start": v(100.68, 21.56) * mm, "end": v(100.68, 27.17) * mm});
            skLineSegment(sketch, "E98.bottom", {"start": v(100.02, 8.72) * mm, "end": v(94.21, 8.72) * mm});
            skLineSegment(sketch, "E98.top", {"start": v(100.02, 14.35) * mm, "end": v(94.21, 14.35) * mm});
            skLineSegment(sketch, "E98.left", {"start": v(100.02, 8.72) * mm, "end": v(100.02, 14.35) * mm});
            skLineSegment(sketch, "E98.right", {"start": v(94.21, 8.72) * mm, "end": v(94.21, 14.35) * mm});
            skLineSegment(sketch, "E99.bottom", {"start": v(100.02, 15.06) * mm, "end": v(94.21, 15.06) * mm});
            skLineSegment(sketch, "E99.top", {"start": v(100.02, 20.7) * mm, "end": v(94.21, 20.7) * mm});
            skLineSegment(sketch, "E99.left", {"start": v(100.02, 15.06) * mm, "end": v(100.02, 20.7) * mm});
            skLineSegment(sketch, "E99.right", {"start": v(94.21, 15.06) * mm, "end": v(94.21, 20.7) * mm});
            skLineSegment(sketch, "E100.bottom", {"start": v(100.02, 21.56) * mm, "end": v(94.21, 21.56) * mm});
            skLineSegment(sketch, "E100.top", {"start": v(100.02, 27.17) * mm, "end": v(94.21, 27.17) * mm});
            skLineSegment(sketch, "E100.left", {"start": v(100.02, 21.56) * mm, "end": v(100.02, 27.17) * mm});
            skLineSegment(sketch, "E100.right", {"start": v(94.21, 21.56) * mm, "end": v(94.21, 27.17) * mm});
            skLineSegment(sketch, "E101.bottom", {"start": v(93.63, 39.12) * mm, "end": v(113.63, 39.12) * mm});
            skLineSegment(sketch, "E101.top", {"start": v(93.63, 59.12) * mm, "end": v(113.63, 59.12) * mm});
            skLineSegment(sketch, "E101.left", {"start": v(93.63, 39.12) * mm, "end": v(93.63, 59.12) * mm});
            skLineSegment(sketch, "E101.right", {"start": v(113.63, 39.12) * mm, "end": v(113.63, 59.12) * mm});
            skLineSegment(sketch, "E102.bottom", {"start": v(107.24, 39.67) * mm, "end": v(112.84, 39.67) * mm});
            skLineSegment(sketch, "E102.top", {"start": v(107.24, 45.27) * mm, "end": v(112.84, 45.27) * mm});
            skLineSegment(sketch, "E102.left", {"start": v(107.24, 39.67) * mm, "end": v(107.24, 45.27) * mm});
            skLineSegment(sketch, "E102.right", {"start": v(112.84, 39.67) * mm, "end": v(112.84, 45.27) * mm});
            skLineSegment(sketch, "E103.bottom", {"start": v(107.24, 45.98) * mm, "end": v(112.89, 45.98) * mm});
            skLineSegment(sketch, "E103.top", {"start": v(107.24, 51.62) * mm, "end": v(112.89, 51.62) * mm});
            skLineSegment(sketch, "E103.left", {"start": v(107.24, 45.98) * mm, "end": v(107.24, 51.62) * mm});
            skLineSegment(sketch, "E103.right", {"start": v(112.89, 45.98) * mm, "end": v(112.89, 51.62) * mm});
            skLineSegment(sketch, "E104.bottom", {"start": v(107.24, 52.48) * mm, "end": v(112.89, 52.48) * mm});
            skLineSegment(sketch, "E104.top", {"start": v(107.24, 58.1) * mm, "end": v(112.89, 58.1) * mm});
            skLineSegment(sketch, "E104.left", {"start": v(107.24, 52.48) * mm, "end": v(107.24, 58.1) * mm});
            skLineSegment(sketch, "E104.right", {"start": v(112.89, 52.48) * mm, "end": v(112.89, 58.1) * mm});
            skLineSegment(sketch, "E105.bottom", {"start": v(106.6, 45.27) * mm, "end": v(100.94, 45.27) * mm});
            skLineSegment(sketch, "E105.top", {"start": v(106.6, 39.64) * mm, "end": v(100.94, 39.64) * mm});
            skLineSegment(sketch, "E105.left", {"start": v(106.6, 45.27) * mm, "end": v(106.6, 39.64) * mm});
            skLineSegment(sketch, "E105.right", {"start": v(100.94, 45.27) * mm, "end": v(100.94, 39.64) * mm});
            skLineSegment(sketch, "E106.bottom", {"start": v(106.6, 45.98) * mm, "end": v(100.93, 45.98) * mm});
            skLineSegment(sketch, "E106.top", {"start": v(106.6, 51.62) * mm, "end": v(100.93, 51.62) * mm});
            skLineSegment(sketch, "E106.left", {"start": v(106.6, 45.98) * mm, "end": v(106.6, 51.62) * mm});
            skLineSegment(sketch, "E106.right", {"start": v(100.93, 45.98) * mm, "end": v(100.93, 51.62) * mm});
            skLineSegment(sketch, "E107.bottom", {"start": v(106.6, 52.48) * mm, "end": v(100.93, 52.48) * mm});
            skLineSegment(sketch, "E107.top", {"start": v(106.6, 58.1) * mm, "end": v(100.93, 58.1) * mm});
            skLineSegment(sketch, "E107.left", {"start": v(106.6, 52.48) * mm, "end": v(106.6, 58.1) * mm});
            skLineSegment(sketch, "E107.right", {"start": v(100.93, 52.48) * mm, "end": v(100.93, 58.1) * mm});
            skLineSegment(sketch, "E108.bottom", {"start": v(100.28, 39.64) * mm, "end": v(94.47, 39.64) * mm});
            skLineSegment(sketch, "E108.top", {"start": v(100.28, 45.27) * mm, "end": v(94.47, 45.27) * mm});
            skLineSegment(sketch, "E108.left", {"start": v(100.28, 39.64) * mm, "end": v(100.28, 45.27) * mm});
            skLineSegment(sketch, "E108.right", {"start": v(94.47, 39.64) * mm, "end": v(94.47, 45.27) * mm});
            skLineSegment(sketch, "E109.bottom", {"start": v(100.28, 45.98) * mm, "end": v(94.47, 45.98) * mm});
            skLineSegment(sketch, "E109.top", {"start": v(100.28, 51.62) * mm, "end": v(94.47, 51.62) * mm});
            skLineSegment(sketch, "E109.left", {"start": v(100.28, 45.98) * mm, "end": v(100.28, 51.62) * mm});
            skLineSegment(sketch, "E109.right", {"start": v(94.47, 45.98) * mm, "end": v(94.47, 51.62) * mm});
            skLineSegment(sketch, "E110.bottom", {"start": v(100.28, 52.48) * mm, "end": v(94.47, 52.48) * mm});
            skLineSegment(sketch, "E110.top", {"start": v(100.28, 58.1) * mm, "end": v(94.47, 58.1) * mm});
            skLineSegment(sketch, "E110.left", {"start": v(100.28, 52.48) * mm, "end": v(100.28, 58.1) * mm});
            skLineSegment(sketch, "E110.right", {"start": v(94.47, 52.48) * mm, "end": v(94.47, 58.1) * mm});
            skSolve(sketch);
        }
        {
            var Q0;
            Q0 = qSketchRegion(id + "F11", true);
            extrude(context, id + "F12", {"entities" : qUnion([Q0]), "operationType" : NewBodyOperationType.ADD, "depth" : 2 * mm, "offsetDistance" : 25 * mm});
        }
        {
            var Q0;
            Q0=makeQuery(id+"F7.imprint","IMPRINT",FACE,{"disambiguationData":[TD([[makeQuery(id+"F7.imprint","IMPRINT",EDGE,{"derivedFrom":sQuery(id+"F7.wireOp",EDGE,"E40.bottom")}),1.0]])]});
            var Q1;
            Q1=makeQuery(id+"F7.imprint","IMPRINT",FACE,{"disambiguationData":[TD([[makeQuery(id+"F7.imprint","IMPRINT",EDGE,{"derivedFrom":sQuery(id+"F7.wireOp",EDGE,"E41.bottom")}),1.0]])]});
            var Q2;
            Q2=makeQuery(id+"F7.imprint","IMPRINT",FACE,{"disambiguationData":[TD([[makeQuery(id+"F7.imprint","IMPRINT",EDGE,{"derivedFrom":sQuery(id+"F7.wireOp",EDGE,"E42.bottom")}),1.0]])]});
            extrude(context, id + "F13", {"entities" : qUnion([Q0, Q1, Q2]), "operationType" : NewBodyOperationType.ADD, "depth" : 7 * mm, "offsetDistance" : 25 * mm});
        }
        {
            var Q0;
            Q0=makeQuery(id+"F13.opExtrude","CAP_FACE",FACE,{"disambiguationData":[OSD([sQuery(id+"F7.wireOp",EDGE,"E40.bottom"),sQuery(id+"F7.wireOp",EDGE,"E40.top"),sQuery(id+"F7.wireOp",EDGE,"E40.left"),sQuery(id+"F7.wireOp",EDGE,"E40.right"),sQuery(id+"F7.wireOp",EDGE,"q38TVCfY-SBXk-BkvN-aXH4-tpBpDbhZXtqT.bottom"),sQuery(id+"F7.wireOp",EDGE,"q38TVCfY-SBXk-BkvN-aXH4-tpBpDbhZXtqT.top"),sQuery(id+"F7.wireOp",EDGE,"q38TVCfY-SBXk-BkvN-aXH4-tpBpDbhZXtqT.left"),sQuery(id+"F7.wireOp",EDGE,"q38TVCfY-SBXk-BkvN-aXH4-tpBpDbhZXtqT.right")])],"isStart":false});
            var sketch = newSketch(context, id + "F14", { "sketchPlane" : qUnion([Q0])});
            skLineSegment(sketch, "E111.bottom", {"start": v(-134.35, -123.96) * mm, "end": v(-153.7, -123.96) * mm});
            skLineSegment(sketch, "E111.top", {"start": v(-134.35, 107.27) * mm, "end": v(-153.7, 107.27) * mm});
            skLineSegment(sketch, "E111.left", {"start": v(-134.35, -123.96) * mm, "end": v(-134.35, 107.27) * mm});
            skLineSegment(sketch, "E111.right", {"start": v(-153.7, -123.96) * mm, "end": v(-153.7, 107.27) * mm});
            skLineSegment(sketch, "E112.bottom", {"start": v(-166.25, -124.63) * mm, "end": v(-185.36, -124.63) * mm});
            skLineSegment(sketch, "E112.top", {"start": v(-166.25, 107.27) * mm, "end": v(-185.36, 107.27) * mm});
            skLineSegment(sketch, "E112.left", {"start": v(-166.25, -124.63) * mm, "end": v(-166.25, 107.27) * mm});
            skLineSegment(sketch, "E112.right", {"start": v(-185.36, -124.63) * mm, "end": v(-185.36, 107.27) * mm});
            skLineSegment(sketch, "E113.bottom", {"start": v(-100.79, -123.96) * mm, "end": v(-120.15, -123.96) * mm});
            skLineSegment(sketch, "E113.top", {"start": v(-100.79, 107.27) * mm, "end": v(-120.15, 107.27) * mm});
            skLineSegment(sketch, "E113.left", {"start": v(-100.79, -123.96) * mm, "end": v(-100.79, 107.27) * mm});
            skLineSegment(sketch, "E113.right", {"start": v(-120.15, -123.96) * mm, "end": v(-120.15, 107.27) * mm});
            skSolve(sketch);
        }
        {
            var Q0;
            Q0=makeQuery(id+"F14.imprint","IMPRINT",FACE,{"disambiguationData":[TD([[makeQuery(id+"F14.imprint","IMPRINT",EDGE,{"derivedFrom":makeQuery(id+"F13.opExtrude","CAP_EDGE",EDGE,{"disambiguationData":[OSD([sQuery(id+"F7.wireOp",EDGE,"E40.bottom")])],"isStart":false})}),1.0]])]});
            var Q1;
            Q1=makeQuery(id+"F14.imprint","IMPRINT",FACE,{"disambiguationData":[TD([[makeQuery(id+"F14.imprint","IMPRINT",EDGE,{"derivedFrom":sQuery(id+"F14.wireOp",EDGE,"6c4f990a-1257-40e4-ada5-027e77428c3a.top")}),1.0]])]});
            var Q2;
            Q2=makeQuery(id+"F14.imprint","IMPRINT",FACE,{"disambiguationData":[TD([[makeQuery(id+"F14.imprint","IMPRINT",EDGE,{"derivedFrom":sQuery(id+"F14.wireOp",EDGE,"E112.bottom")}),-1.0]])]});
            var Q3;
            Q3=makeQuery(id+"F14.imprint","IMPRINT",FACE,{"disambiguationData":[TD([[makeQuery(id+"F14.imprint","IMPRINT",EDGE,{"derivedFrom":sQuery(id+"F14.wireOp",EDGE,"E111.bottom")}),-1.0]])]});
            var Q4;
            Q4=makeQuery(id+"F14.imprint","IMPRINT",FACE,{"disambiguationData":[TD([[makeQuery(id+"F14.imprint","IMPRINT",EDGE,{"derivedFrom":sQuery(id+"F14.wireOp",EDGE,"E113.bottom")}),-1.0]])]});
            extrude(context, id + "F15", {"entities" : qUnion([Q0, Q1, Q2, Q3, Q4]), "operationType" : NewBodyOperationType.ADD, "depth" : 130 * mm, "offsetDistance" : 25 * mm});
        }
        {
            var Q0;
            Q0=makeQuery(id+"F7.imprint","IMPRINT",FACE,{"disambiguationData":[TD([[makeQuery(id+"F7.imprint","IMPRINT",EDGE,{"derivedFrom":sQuery(id+"F7.wireOp",EDGE,"E43.bottom")}),1.0]])]});
            extrude(context, id + "F16", {"entities" : qUnion([Q0]), "operationType" : NewBodyOperationType.ADD, "depth" : 15 * mm, "offsetDistance" : 25 * mm});
        }
        {
            var Q0;
            {var subQ1=sQuery(id+"F7.wireOp",EDGE,"E47.bottom");Q0=makeQuery(id+"F7.imprint","IMPRINT",FACE,{"disambiguationData":[TD([[makeQuery(id+"F7.imprint","IMPRINT",EDGE,{"derivedFrom":subQ1}),1.0]])]});}
            var Q1;
            Q1=makeQuery(id+"F7.imprint","IMPRINT",FACE,{"disambiguationData":[TD([[makeQuery(id+"F7.imprint","IMPRINT",EDGE,{"derivedFrom":sQuery(id+"F7.wireOp",EDGE,"E46.bottom")}),1.0]])]});
            var Q2;
            Q2=makeQuery(id+"F7.imprint","IMPRINT",FACE,{"disambiguationData":[TD([[makeQuery(id+"F7.imprint","IMPRINT",EDGE,{"derivedFrom":sQuery(id+"F7.wireOp",EDGE,"E45.bottom")}),1.0]])]});
            var Q3;
            Q3=makeQuery(id+"F7.imprint","IMPRINT",FACE,{"disambiguationData":[TD([[makeQuery(id+"F7.imprint","IMPRINT",EDGE,{"derivedFrom":sQuery(id+"F7.wireOp",EDGE,"E44.bottom")}),1.0]])]});
            extrude(context, id + "F17", {"entities" : qUnion([Q0, Q1, Q2, Q3]), "operationType" : NewBodyOperationType.ADD, "depth" : 8 * mm, "offsetDistance" : 25 * mm});
        }
        {
            var Q0;
            Q0=makeQuery(id+"F1.opExtrude","CAP_FACE",FACE,{"disambiguationData":[OSD([sQuery(id+"F0.wireOp",EDGE,"E0.bottom"),sQuery(id+"F0.wireOp",EDGE,"E0.top"),sQuery(id+"F0.wireOp",EDGE,"E0.left"),sQuery(id+"F0.wireOp",EDGE,"E0.right"),sQuery(id+"F0.wireOp",EDGE,"E2.bottom"),sQuery(id+"F0.wireOp",EDGE,"E2.top"),sQuery(id+"F0.wireOp",EDGE,"E2.left"),sQuery(id+"F0.wireOp",EDGE,"E2.right"),sQuery(id+"F0.wireOp",EDGE,"E3"),sQuery(id+"F0.wireOp",EDGE,"E4"),sQuery(id+"F0.wireOp",EDGE,"E5"),sQuery(id+"F0.wireOp",EDGE,"E6"),sQuery(id+"F0.wireOp",EDGE,"E7"),sQuery(id+"F0.wireOp",EDGE,"E8"),sQuery(id+"F0.wireOp",EDGE,"E9")])],"isStart":true});
            var sketch = newSketch(context, id + "F18", { "sketchPlane" : qUnion([Q0])});
            skCircle(sketch, "E114", {"center": v(-209.47, 113.98) * mm, "radius": 3 * mm});
            skCircle(sketch, "E115", {"center": v(169.91, 126.81) * mm, "radius": 3 * mm});
            skCircle(sketch, "E116", {"center": v(-203.84, -95.7) * mm, "radius": 3 * mm});
            skCircle(sketch, "E117", {"center": v(169.8, -109.27) * mm, "radius": 3 * mm});
            skSolve(sketch);
        }
        {
            var Q0;
            Q0 = qSketchRegion(id + "F18", true);
            extrude(context, id + "F19", {"entities" : qUnion([Q0]), "operationType" : NewBodyOperationType.ADD, "depth" : 15 * mm, "offsetDistance" : 25 * mm});
        }
        {
            var Q0;
            Q0=makeQuery(id+"F19.opExtrude","CAP_FACE",FACE,{"disambiguationData":[OSD([sQuery(id+"F18.wireOp",EDGE,"E114")])],"isStart":false});
            var sketch = newSketch(context, id + "F20", { "sketchPlane" : qUnion([Q0])});
            skCircle(sketch, "E118", {"center": v(-209.47, 113.98) * mm, "radius": 6 * mm});
            skCircle(sketch, "E119", {"center": v(-203.82, -95.69) * mm, "radius": 6 * mm});
            skCircle(sketch, "E120", {"center": v(169.8, -109.25) * mm, "radius": 6 * mm});
            skCircle(sketch, "E121", {"center": v(169.9, 126.83) * mm, "radius": 6 * mm});
            skSolve(sketch);
        }
        {
            var Q0;
            Q0 = qSketchRegion(id + "F20", true);
            var Q1;
            Q1 = qSketchRegion(id + "F22", true);
            extrude(context, id + "F21", {"entities" : qUnion([Q0, Q1]), "operationType" : NewBodyOperationType.ADD, "depth" : 5 * mm, "offsetDistance" : 25 * mm});
        }
    });
